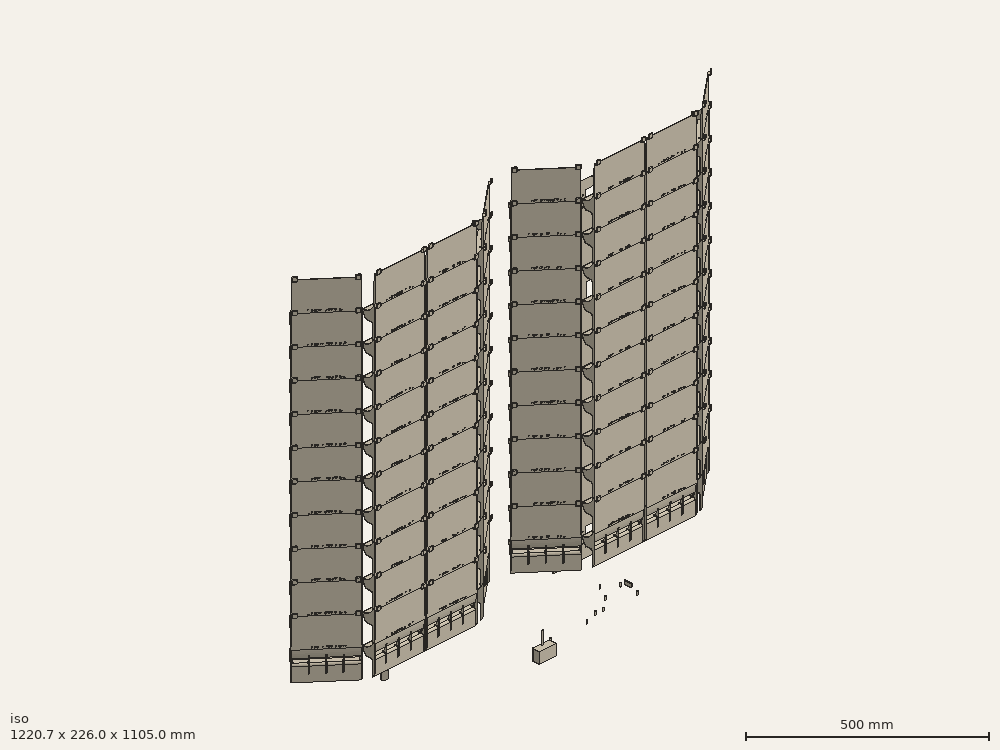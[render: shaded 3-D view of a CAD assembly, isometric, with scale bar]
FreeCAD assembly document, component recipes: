
FREECAD ASSEMBLY — COMPONENT RECIPES ("composit_stand11")

This assembly document has 29 components, labeled P0..P28 below (a component is one placed body or linked part). 28 of them carry a construction recipe — the FreeCAD feature program that regenerates the part from scratch, quoted from this document or its linked companion documents; the rest are supplied as boundary geometry only. No exploded tour is included for this assembly.
NOTE — this tour is split across 2 documents so each fits a 32k-token context. This is document 1: the component sections continue in the remaining 1 document, each repeating the header above.
COMPONENT P0 — recipe-attached ("dropper_fix_composit", modeled in this document).
Construction recipe (the document's own serialized feature program — sketch geometry with constraints, then the solid features built on it; lengths are millimeters unless a unit is written):

FEATURE [PartDesign::SubShapeBinder] Binder003
  BindCopyOnChange = 0
  BindMode = 0
  ClaimChildren = true
  Context = -> Body002 [Binder003.]
  Fuse = false
  MakeFace = true
  OffsetFill = false
  OffsetIntersection = false
  OffsetJoinType = 0
  OffsetOpenResult = false
  PartialLoad = false
  Relative = true
  Support = -> [Connect001]
  _Version = 2
FEATURE [PartDesign::FeaturePython] BaseBend001  # WARN: FeaturePython — macro-defined, semantics opaque (R4)
  BendSide = 0
  BendSketch = -> Binder003
  MidPlane = false
  Reverse = false
  Suppressed = false
  length = 100
  radius = 0.1
  thickness = 0.3
FEATURE [PartDesign::FeaturePython] Extend001  # WARN: FeaturePython — macro-defined, semantics opaque (R4)
  BaseFeature = -> BaseBend001
  Offset = 0.02
  Refine = true
  Suppressed = false
  UseSubtraction = false
  baseObject = -> BaseBend001 [Face1]
  gap1 = 0
  gap2 = 0
  length = 0
FEATURE [PartDesign::FeaturePython] Bend001  # WARN: FeaturePython — macro-defined, semantics opaque (R4)
  AutoMiter = true
  BaseFeature = -> Extend001
  BendType = 1
  LengthList = [15]
  LengthSpec = 0
  ReliefFactor = 0.7
  Suppressed = false
  UseReliefFactor = false
  angle = 90
  baseObject = -> Extend001 [Edge6,Edge8,Edge9,Edge11]
  bendAList = [90]
  extend1 = 0
  extend2 = 0
  gap1 = 0
  gap2 = 0
  invert = true
  kfactor = 0.5
  length = 15
  maxExtendDist = 5
  minGap = 0.2
  minReliefGap = 1
  miterangle1 = 0
  miterangle2 = 0
  offset = 0
  radius = 0.1
  reliefType = 0
  reliefd = 1
  reliefw = 0.8
  sketchflip = false
  sketchinvert = false
  unfold = false
  expr: radius = BaseBend.radius
FEATURE [Sketcher::SketchObject] Sketch031
  AttachmentSupport = -> [XY_Plane003]
  ExternalGeometry = -> [Binder003]
  FullyConstrained = true
  MapMode = 5
  sketch-geometry (13):
    g0: LineSegment StartX=172.194 StartY=8.2 StartZ=0 EndX=172.194 EndY=11.2 EndZ=0
    g1: LineSegment StartX=172.194 StartY=11.2 StartZ=0 EndX=174.122 EndY=8.90187 EndZ=0
    g2: LineSegment StartX=172.194 StartY=8.2 StartZ=0 EndX=173.286 EndY=8.2 EndZ=0
    g3: LineSegment StartX=173.286 StartY=8.2 StartZ=0 EndX=174.122 EndY=8.90187 EndZ=0
    g4: LineSegment StartX=309.163 StartY=122.737 StartZ=0 EndX=309.163 EndY=147 EndZ=0
    g5: LineSegment StartX=309.163 StartY=122.214 StartZ=0 EndX=312.42 EndY=124.947 EndZ=0
    g6: LineSegment StartX=309.163 StartY=122.214 StartZ=0 EndX=308.906 EndY=122.521 EndZ=0
    g7: LineSegment StartX=308.906 StartY=122.521 StartZ=0 EndX=309.163 EndY=122.737 EndZ=0
    g8: LineSegment StartX=312.163 StartY=150 StartZ=0 EndX=312.163 EndY=125.254 EndZ=0
    g9: LineSegment StartX=312.163 StartY=125.254 StartZ=0 EndX=312.42 EndY=124.947 EndZ=0
    g10: LineSegment StartX=309.163 StartY=147 StartZ=0 EndX=311.763 EndY=147 EndZ=0
    g11: LineSegment StartX=311.763 StartY=147 StartZ=0 EndX=311.763 EndY=150 EndZ=0
    g12: LineSegment StartX=311.763 StartY=150 StartZ=0 EndX=312.163 EndY=150 EndZ=0
  constraints (38):
    c: PointOnObject(g0,g-3)
    c: Coincident(g0,g1)
    c: PointOnObject(g1,g-4)
    c: Perpendicular(g-3,g0)
    c: Perpendicular(g-4,g1)
    c: Equal(g1,g0)
    c: DistanceY(g0,g0) = 3
    c: Coincident(g0,g2)
    c: Coincident(g2,g-4)
    c: Coincident(g2,g3)
    c: Coincident(g3,g1)
    c: Vertical(g4)
    c: Coincident(g4,g10)
    c: Coincident(g12,g8)
    c: PointOnObject(g5,g-4)
    c: Vertical(g4,g5)
    c: Coincident(g5,g6)
    c: Coincident(g6,g7)
    c: Distance(g6) = 0.4
    c: Perpendicular(g5,g6)
    c: Perpendicular(g7,g6)
    c: DistanceX(g10,g12) = 3
    c: Coincident(g5,g9)
    c: Coincident(g7,g4)
    c: Coincident(g8,g9)
    c: Vertical(g8)
    c: Perpendicular(g5,g9)
    c: PointOnObject(g-5,g5)
    c: Distance(g9) = 0.4
    c: Coincident(g10,g11)
    c: Horizontal(g10)
    c: Coincident(g11,g12)
    c: Horizontal(g12)
    c: Coincident(g8,g-5)
    c: Vertical(g11)
    c: DistanceY(g11,g11) = 3
    c: DistanceX(g12,g12) = 0.4
    c: Distance(g8,g4) = 3
FEATURE [PartDesign::Pocket] Pocket003
  BaseFeature = -> Bend001
  Direction = (0,0,-1)
  Length = 5
  Length2 = 5
  Midplane = true
  Profile = -> Sketch031
  ReferenceAxis = -> Sketch031 [N_Axis]
  Suppressed = false
  Type = 1
FEATURE [PartDesign::Mirrored] Mirrored
  BaseFeature = -> Pocket003
  MirrorPlane = -> Sketch031 [V_Axis]
  Originals = -> [Pocket003]
  Suppressed = false
FEATURE [PartDesign::CoordinateSystem] Local_CS008
  AttacherType = Attacher::AttachEngine3D
  AttachmentOffset = pos=(0,20,0) rot=(0,0,1;0rad)
  AttachmentSupport = -> [XY_Plane003]
  MapMode = 5
  Placement = pos=(0,20,0) rot=(0,0,1;0rad)
  expr: .AttachmentOffset.Base.y = <<base_Sketch>>.Constraints.offset
FEATURE [PartDesign::CoordinateSystem] Local_CS013  label="dropper_fix_PP_placement"
  AttacherType = Attacher::AttachEngine3D
  AttachmentOffset = pos=(0,0,3) rot=(0,0,1;0rad)
  AttachmentSupport = -> [XY_Plane003]
  MapMode = 5
  Placement = pos=(0,0,3) rot=(0,0,1;0rad)
FEATURE [PartDesign::Boolean] Boolean031
  BaseFeature = -> Mirrored
  Group = -> [Compound039]
  Suppressed = false
  Type = 1
  UsePlacement = true
FEATURE [PartDesign::Boolean] Boolean030
  BaseFeature = -> Boolean031
  Group = -> [Compound038]
  Refine = true
  Suppressed = false
  Type = 0
  UsePlacement = true
FEATURE [PartDesign::Boolean] Boolean002
  BaseFeature = -> Boolean030
  Group = -> [Compound009]
  Suppressed = false
  Type = 1
  UsePlacement = true
FEATURE [PartDesign::Body] Body002  label="dropper_fix_composit"
  Group = -> [Binder003,BaseBend001,Extend001,Sketch031,Bend001,Pocket003,Mirrored,Boolean031,Boolean030,Boolean002,Local_CS008,Local_CS013]
  Origin = -> Origin003
  Tip = -> Boolean002
COMPONENT P1 — recipe-attached ("sink", modeled in this document).
Construction recipe (the document's own serialized feature program — sketch geometry with constraints, then the solid features built on it; lengths are millimeters unless a unit is written):

FEATURE [PartDesign::SubShapeBinder] Binder001
  BindCopyOnChange = 0
  BindMode = 0
  ClaimChildren = true
  Context = -> Body003 [Binder001.]
  Fuse = false
  MakeFace = true
  OffsetFill = false
  OffsetIntersection = false
  OffsetJoinType = 0
  OffsetOpenResult = false
  PartialLoad = false
  Relative = false
  Support = -> [Sketch]
  _Version = 2
FEATURE [PartDesign::CoordinateSystem] Local_CS
  AttacherType = Attacher::AttachEngine3D
  AttachmentOffset = pos=(0,0,0) rot=(0,1,0;1.5708rad)
  MapMode = 7
  Placement = pos=(164.635,-1.4e-14,0) rot=(0.889126,0.323616,0.323616;1.68804rad)
FEATURE [Sketcher::SketchObject] Sketch005  label="sink_side_line"
  ExternalGeometry = -> [Binder001]
  FullyConstrained = true
  MapMode = 5
  Placement = pos=(164.635,-2.8e-14,0) rot=(0.889126,0.323616,0.323616;1.68804rad)
  sketch-geometry (1):
    g0: LineSegment StartX=-2.84e-14 StartY=0 StartZ=0 EndX=202.244 EndY=20 EndZ=0
  constraints (4):
    c: Coincident(g0,g-3)
    c: Vertical(g0,g-3)
    c: DistanceY(g0) = 20  'height'
    c: Angle(g0) = 0.0985699  'angle'
FEATURE [Sketcher::SketchObject] Sketch006  label="sink_front_bend_sketch"
  ExternalGeometry = -> [Sketch005]
  FullyConstrained = true
  MapMode = 5
  Placement = pos=(0,0,0) rot=(0.57735,0.57735,0.57735;2.0944rad)
  sketch-geometry (3):
    g0: LineSegment StartX=0 StartY=2.91403 StartZ=0 EndX=-1.83e-14 EndY=0 EndZ=0
    g1: LineSegment StartX=-1.83e-14 StartY=0 StartZ=0 EndX=2.88014 EndY=0.443099 EndZ=0
    g2: ArcOfCircle CenterX=2.5 CenterY=2.91403 CenterZ=0 NormalX=0 NormalY=0 NormalZ=1 AngleXU=0 Radius=2.5 StartAngle=3.14159 EndAngle=4.86504
  constraints (8):
    c: PointOnObject(g0,g-2)
    c: Coincident(g0,g-3)
    c: Coincident(g0,g1)
    c: PointOnObject(g1,g-3)
    c: Tangent(g2,g1) = -1.5708
    c: Tangent(g2,g0) = -1.5708
    c: Radius(g2) = 2.5
    c: Angle(g1) = 0.152649  'angle'
FEATURE [Sketcher::SketchObject] Sketch007
  ExternalGeometry = -> [Binder001]
  FullyConstrained = true
  MapMode = 7
  Placement = pos=(164.635,-8.5e-14,-4e-15) rot=(0.846388,-0.394677,-0.357572;1.83324rad)
  sketch-geometry (3):
    g0: ArcOfCircle CenterX=-2.5 CenterY=2.81034 CenterZ=0 NormalX=0 NormalY=0 NormalZ=1 AngleXU=0 Radius=2.5 StartAngle=4.59564 EndAngle=6.28319
    g1: LineSegment StartX=-2.79121 StartY=0.327355 StartZ=0 EndX=0 EndY=0 EndZ=0
    g2: LineSegment StartX=0 StartY=0 StartZ=0 EndX=0 EndY=2.81034 EndZ=0
  constraints (7):
    c: PointOnObject(g0,g-2)
    c: Coincident(g1,g-1)
    c: Coincident(g2,g1)
    c: Tangent(g2,g0) = -1.5708
    c: Tangent(g1,g0) = -1.5708
    c: PointOnObject(g0,g-3)
    c: Radius(g0) = 2.5
FEATURE [PartDesign::CoordinateSystem] Local_CS001
  AttacherType = Attacher::AttachEngine3D
  AttachmentOffset = pos=(0,0,0) rot=(1,0,0;0.152649rad)
  MapMode = 5
  Placement = pos=(0,0,0) rot=(1,0,0;0.152649rad)
  expr: .AttachmentOffset.Rotation.Angle = <<sink_front_bend_sketch>>.Constraints.angle
FEATURE [Sketcher::SketchObject] Sketch008  label="sink_plane_sketch"
  ExternalGeometry = -> [Sketch006,Sketch005,Sketch007]
  FullyConstrained = true
  MapMode = 5
  Placement = pos=(0,0,0) rot=(1,0,0;0.152649rad)
  sketch-geometry (4):
    g0: LineSegment StartX=-163.725 StartY=2.91403 StartZ=0 EndX=163.725 EndY=2.91403 EndZ=0
    g1: LineSegment StartX=163.725 StartY=2.91403 StartZ=0 EndX=317.576 EndY=133.529 EndZ=0
    g2: LineSegment StartX=317.576 StartY=133.529 StartZ=0 EndX=-317.576 EndY=133.529 EndZ=0
    g3: LineSegment StartX=-317.576 StartY=133.529 StartZ=0 EndX=-163.725 EndY=2.91403 EndZ=0
  constraints (14):
    c: Coincident(g0,g1)
    c: Coincident(g1,g2)
    c: Coincident(g2,g3)
    c: Coincident(g3,g0)
    c: Symmetric(g0,g0,g-2)
    c: Symmetric(g2,g1,g-2)
    c: Parallel(g1,g-4)
    c: PointOnObject(g-5,g1)
    c: PointOnObject(g-3,g0)
    c: Distance(g1) = 201.818  'rigth_side'
    c: Distance(g0) = 327.45  'front'
    c: Distance(g2) = 635.153  'end'
    c: Distance(g3) = 201.818  'left_side'
    c: DistanceY(g-4,g1) = 2
FEATURE [Sketcher::SketchObject] Sketch009
  ExternalGeometry = -> [Sketch006]
  FullyConstrained = true
  MapMode = 2
  Placement = pos=(0,0,0) rot=(0.57735,0.57735,0.57735;2.0944rad)
  sketch-geometry (4):
    g0: ArcOfCircle CenterX=2.5 CenterY=2.91403 CenterZ=0 NormalX=0 NormalY=0 NormalZ=1 AngleXU=0 Radius=2.5 StartAngle=3.14159 EndAngle=4.86504
    g1: LineSegment StartX=2.88014 StartY=0.443099 StartZ=0 EndX=2.80411 EndY=0.937285 EndZ=0
    g2: LineSegment StartX=1.1302e-12 StartY=2.91403 StartZ=0 EndX=0.5 EndY=2.91403 EndZ=0
    g3: ArcOfCircle CenterX=2.5 CenterY=2.91403 CenterZ=0 NormalX=0 NormalY=0 NormalZ=1 AngleXU=0 Radius=2 StartAngle=3.14159 EndAngle=4.86504
  constraints (10):
    c: Coincident(g0,g-3)
    c: Tangent(g0,g-3) = -1.5708
    c: Coincident(g0,g1)
    c: Coincident(g0,g2)
    c: Coincident(g3,g0)
    c: Coincident(g3,g2)
    c: Coincident(g3,g1)
    c: Perpendicular(g3,g1)
    c: Perpendicular(g3,g2)
    c: Distance(g1) = 0.5
FEATURE [Sketcher::SketchObject] Sketch010
  ExternalGeometry = -> [Sketch007]
  FullyConstrained = true
  MapMode = 7
  Placement = pos=(163.725,2.88014,0.443099) rot=(0.846388,-0.394677,-0.357572;1.83324rad)
  sketch-geometry (4):
    g0: ArcOfCircle CenterX=0.291206 CenterY=2.48298 CenterZ=0 NormalX=0 NormalY=0 NormalZ=1 AngleXU=0 Radius=2.5 StartAngle=4.59564 EndAngle=6.28319
    g1: LineSegment StartX=-2.56e-14 StartY=2.7e-15 StartZ=0 EndX=0.0582413 EndY=0.496596 EndZ=0
    g2: LineSegment StartX=2.79121 StartY=2.48298 StartZ=0 EndX=2.29121 EndY=2.48298 EndZ=0
    g3: ArcOfCircle CenterX=0.291206 CenterY=2.48298 CenterZ=0 NormalX=0 NormalY=0 NormalZ=1 AngleXU=0 Radius=2 StartAngle=4.59564 EndAngle=6.28319
  constraints (10):
    c: Coincident(g0,g-3)
    c: Tangent(g0,g-3) = -1.5708
    c: Coincident(g1,g0)
    c: Coincident(g2,g0)
    c: Coincident(g3,g0)
    c: Coincident(g3,g1)
    c: Coincident(g3,g2)
    c: Perpendicular(g0,g1)
    c: Perpendicular(g0,g2)
    c: Distance(g1) = 0.5
FEATURE [Sketcher::SketchObject] Sketch011
  ExternalGeometry = -> [Sketch008]
  FullyConstrained = true
  MapMode = 7
  Placement = pos=(-163.725,2.88014,0.443099) rot=(-0.298783,0.640743,0.707232;3.7787rad)
  sketch-geometry (4):
    g0: ArcOfCircle CenterX=0.291206 CenterY=2.48298 CenterZ=0 NormalX=0 NormalY=0 NormalZ=1 AngleXU=0 Radius=2 StartAngle=4.59564 EndAngle=6.28319
    g1: ArcOfCircle CenterX=0.291206 CenterY=2.48298 CenterZ=0 NormalX=0 NormalY=0 NormalZ=1 AngleXU=0 Radius=2.5 StartAngle=4.59564 EndAngle=6.28319
    g2: LineSegment StartX=-4e-16 StartY=0 StartZ=0 EndX=0.0582413 EndY=0.496596 EndZ=0
    g3: LineSegment StartX=2.29121 StartY=2.48298 StartZ=0 EndX=2.79121 EndY=2.48298 EndZ=0
  constraints (12):
    c: Coincident(g1,g0)
    c: Coincident(g1,g-1)
    c: Coincident(g2,g1)
    c: Coincident(g2,g0)
    c: Coincident(g3,g0)
    c: Coincident(g3,g1)
    c: Perpendicular(g0,g3)
    c: Perpendicular(g0,g2)
    c: Perpendicular(g2,g-3)
    c: Horizontal(g3)
    c: Radius(g0) = 2
    c: Distance(g2) = 0.5
FEATURE [PartDesign::Pad] Pad
  Direction = (0,-0.152057,0.988372)
  Length = 0.5
  Length2 = 10
  Placement = pos=(0,0,0) rot=(1,0,0;0.152649rad)
  Profile = -> Sketch008
  ReferenceAxis = -> Sketch008 [N_Axis]
  Suppressed = false
  Type = 0
FEATURE [PartDesign::Pad] Pad001
  BaseFeature = -> Pad
  Direction = (-0.762326,-0.639667,-0.0984104)
  Length = 201.818
  Length2 = 10
  Placement = pos=(0,0,0) rot=(1,0,0;0.152649rad)
  Profile = -> Sketch010
  ReferenceAxis = -> Sketch010 [N_Axis]
  Reversed = true
  Suppressed = false
  Type = 0
  expr: Length = <<sink_plane_sketch>>.Constraints.rigth_side
FEATURE [PartDesign::Pad] Pad002
  BaseFeature = -> Pad001
  Direction = (-0.762326,0.639667,0.0984104)
  Length = 201.818
  Length2 = 10
  Placement = pos=(0,0,0) rot=(1,0,0;0.152649rad)
  Profile = -> Sketch011
  ReferenceAxis = -> Sketch011 [N_Axis]
  Suppressed = false
  Type = 0
  expr: Length = <<sink_plane_sketch>>.Constraints.left_side
FEATURE [PartDesign::Pad] Pad003
  BaseFeature = -> Pad002
  Direction = (1,0,0)
  Length = 327.45
  Length2 = 10
  Midplane = true
  Placement = pos=(0,0,0) rot=(1,0,0;0.152649rad)
  Profile = -> Sketch009
  ReferenceAxis = -> Sketch009 [N_Axis]
  Suppressed = false
  Type = 0
  expr: Length = <<sink_plane_sketch>>.Constraints.front
FEATURE [Sketcher::SketchObject] Sketch013
  ExternalGeometry = -> [Sketch008,Sketch009]
  FullyConstrained = true
  MapMode = 5
  Placement = pos=(0,0,0) rot=(1,0,0;1.5708rad)
  sketch-geometry (6):
    g0: LineSegment StartX=-163.725 StartY=2.91403 StartZ=0 EndX=-163.725 EndY=80 EndZ=0
    g1: LineSegment StartX=-163.725 StartY=80 StartZ=0 EndX=163.725 EndY=80 EndZ=0
    g2: LineSegment StartX=163.725 StartY=80 StartZ=0 EndX=163.725 EndY=2.91403 EndZ=0
    g3: LineSegment StartX=163.725 StartY=2.91403 StartZ=0 EndX=-163.725 EndY=2.91403 EndZ=0
    g4: LineSegment StartX=-163.725 StartY=0.443099 StartZ=0 EndX=-163.725 EndY=2.91403 EndZ=0
    g5: LineSegment StartX=163.725 StartY=0.443099 StartZ=0 EndX=163.725 EndY=2.91403 EndZ=0
  constraints (16):
    c: Vertical(g0)
    c: Coincident(g0,g1)
    c: Horizontal(g1)
    c: Coincident(g1,g2)
    c: Vertical(g2)
    c: Coincident(g2,g3)
    c: Coincident(g3,g0)
    c: Horizontal(g3)
    c: PointOnObject(g-4,g3)
    c: Coincident(g4,g-3)
    c: Coincident(g4,g0)
    c: Perpendicular(g3,g4)
    c: Coincident(g5,g-3)
    c: Coincident(g5,g2)
    c: Perpendicular(g3,g5)
    c: DistanceY(g1) = 80
FEATURE [Sketcher::SketchObject] Sketch012
  ExternalGeometry = -> [Sketch008,Sketch010,Sketch013]
  FullyConstrained = true
  MapMode = 5
  Placement = pos=(164.635,-2.8e-14,0) rot=(0.889126,0.323616,0.323616;1.68804rad)
  sketch-geometry (4):
    g0: LineSegment StartX=0.909926 StartY=2.91403 StartZ=0 EndX=201.749 EndY=22.775 EndZ=0
    g1: LineSegment StartX=0.909926 StartY=2.91403 StartZ=0 EndX=0.909926 EndY=80 EndZ=0
    g2: LineSegment StartX=0.909926 StartY=80 StartZ=0 EndX=201.749 EndY=80 EndZ=0
    g3: LineSegment StartX=201.749 StartY=80 StartZ=0 EndX=201.749 EndY=22.775 EndZ=0
  constraints (11):
    c: Coincident(g0,g-4)
    c: Parallel(g-3,g0)
    c: Equal(g0,g-3)
    c: Coincident(g0,g1)
    c: Vertical(g1)
    c: Coincident(g1,g2)
    c: Horizontal(g2)
    c: Coincident(g2,g3)
    c: Coincident(g3,g0)
    c: Vertical(g3)
    c: Horizontal(g-5,g1)
FEATURE [PartDesign::Pad] Pad004
  BaseFeature = -> Pad003
  Direction = (0,-1,2e-16)
  Length = 0.5
  Length2 = 10
  Placement = pos=(0,0,0) rot=(1,0,0;0.152649rad)
  Profile = -> Sketch013
  ReferenceAxis = -> Sketch013 [N_Axis]
  Reversed = true
  Suppressed = false
  Type = 0
FEATURE [PartDesign::Pad] Pad005
  BaseFeature = -> Pad004
  Direction = (0.642788,-0.766044,0)
  Length = 0.5
  Length2 = 10
  Placement = pos=(0,0,0) rot=(1,0,0;0.152649rad)
  Profile = -> Sketch012
  ReferenceAxis = -> Sketch012 [N_Axis]
  Reversed = true
  Suppressed = false
  Type = 0
FEATURE [Sketcher::SketchObject] Sketch014
  ExternalGeometry = -> [Binder001]
  FullyConstrained = true
  MapMode = 5
  sketch-geometry (1):
    g0: LineSegment StartX=-319.563 StartY=130 StartZ=0 EndX=-164.635 EndY=0 EndZ=0
  constraints (2):
    c: Symmetric(g0,g-3,g-2)
    c: Symmetric(g0,g-3,g-2)
FEATURE [PartDesign::CoordinateSystem] Local_CS003
  AttacherType = Attacher::AttachEngine3D
  AttachmentOffset = pos=(0,0,0) rot=(0,1,0;1.5708rad)
  MapMode = 7
  Placement = pos=(-164.635,-1.4e-14,0) rot=(0.889126,-0.323616,-0.323616;1.68804rad)
FEATURE [Sketcher::SketchObject] Sketch015
  ExternalGeometry = -> [Sketch008,Sketch011,Sketch013]
  FullyConstrained = true
  MapMode = 5
  Placement = pos=(-164.635,-2.8e-14,0) rot=(0.889126,-0.323616,-0.323616;1.68804rad)
  sketch-geometry (5):
    g0: LineSegment StartX=-201.749 StartY=22.775 StartZ=0 EndX=-0.909926 EndY=2.91403 EndZ=0
    g1: LineSegment StartX=-0.909926 StartY=2.91403 StartZ=0 EndX=-0.909926 EndY=80 EndZ=0
    g2: LineSegment StartX=-0.909926 StartY=80 StartZ=0 EndX=-201.749 EndY=80 EndZ=0
    g3: LineSegment StartX=-201.749 StartY=80 StartZ=0 EndX=-201.749 EndY=22.775 EndZ=0
    g4: LineSegment StartX=-201.993 StartY=20.3041 StartZ=0 EndX=-201.749 EndY=22.775 EndZ=0
  constraints (13):
    c: Coincident(g0,g-4)
    c: Coincident(g1,g0)
    c: Vertical(g1)
    c: Coincident(g1,g2)
    c: Horizontal(g2)
    c: Coincident(g2,g3)
    c: Coincident(g3,g0)
    c: Vertical(g3)
    c: Coincident(g4,g-3)
    c: Coincident(g4,g0)
    c: Perpendicular(g-3,g4)
    c: Parallel(g-3,g0)
    c: Horizontal(g1,g-5)
FEATURE [PartDesign::Pad] Pad006
  BaseFeature = -> Pad005
  Direction = (-0.642788,-0.766044,0)
  Length = 0.5
  Length2 = 10
  Placement = pos=(0,0,0) rot=(1,0,0;0.152649rad)
  Profile = -> Sketch015
  ReferenceAxis = -> Sketch015 [N_Axis]
  Reversed = true
  Suppressed = false
  Type = 0
FEATURE [Sketcher::SketchObject] Sketch016
  ExternalGeometry = -> [Pad006]
  FullyConstrained = true
  MapMode = 5
  Placement = pos=(0,0,0) rot=(1,0,0;0.152649rad)
  sketch-geometry (28):
    g0: LineSegment StartX=0 StartY=2 StartZ=0 EndX=40.9313 EndY=2 EndZ=0
    g1: LineSegment StartX=40.9313 StartY=2 StartZ=0 EndX=81.8625 EndY=2 EndZ=0
    g2: LineSegment StartX=81.8625 StartY=2 StartZ=0 EndX=122.794 EndY=2 EndZ=0
    g3: LineSegment StartX=122.794 StartY=2 StartZ=0 EndX=163.725 EndY=2 EndZ=0
    g4: ArcOfCircle CenterX=-17 CenterY=2 CenterZ=0 NormalX=0 NormalY=0 NormalZ=1 AngleXU=0 Radius=3 StartAngle=1.5708 EndAngle=4.71239
    g5: ArcOfCircle CenterX=17 CenterY=2 CenterZ=0 NormalX=0 NormalY=0 NormalZ=1 AngleXU=0 Radius=3 StartAngle=4.71239 EndAngle=7.85398
    g6: LineSegment StartX=-17 StartY=5 StartZ=0 EndX=17 EndY=5 EndZ=0
    g7: LineSegment StartX=-17 StartY=-1 StartZ=0 EndX=17 EndY=-1 EndZ=0
    g8: GeomPoint X=-20 Y=2 Z=0
    g9: GeomPoint X=20 Y=2 Z=0
    g10: ArcOfCircle CenterX=106 CenterY=2 CenterZ=0 NormalX=0 NormalY=0 NormalZ=1 AngleXU=0 Radius=3 StartAngle=1.5708 EndAngle=4.71239
    g11: ArcOfCircle CenterX=140 CenterY=2 CenterZ=0 NormalX=0 NormalY=0 NormalZ=1 AngleXU=0 Radius=3 StartAngle=4.71239 EndAngle=7.85398
    g12: LineSegment StartX=106 StartY=5 StartZ=0 EndX=140 EndY=5 EndZ=0
    g13: LineSegment StartX=106 StartY=-1 StartZ=0 EndX=140 EndY=-1 EndZ=0
    g14: ArcOfCircle CenterX=-140 CenterY=2 CenterZ=0 NormalX=0 NormalY=0 NormalZ=1 AngleXU=0 Radius=3 StartAngle=1.5708 EndAngle=4.71239
    g15: ArcOfCircle CenterX=-106 CenterY=2 CenterZ=0 NormalX=0 NormalY=0 NormalZ=1 AngleXU=0 Radius=3 StartAngle=4.71239 EndAngle=7.85398
    g16: LineSegment StartX=-140 StartY=5 StartZ=0 EndX=-106 EndY=5 EndZ=0
    g17: LineSegment StartX=-140 StartY=-1 StartZ=0 EndX=-106 EndY=-1 EndZ=0
    g18: ArcOfCircle CenterX=-78.5 CenterY=2 CenterZ=0 NormalX=0 NormalY=0 NormalZ=1 AngleXU=0 Radius=3 StartAngle=1.5708 EndAngle=4.71239
    g19: ArcOfCircle CenterX=-44.5 CenterY=2 CenterZ=0 NormalX=0 NormalY=0 NormalZ=1 AngleXU=0 Radius=3 StartAngle=4.71239 EndAngle=7.85398
    g20: LineSegment StartX=-78.5 StartY=5 StartZ=0 EndX=-44.5 EndY=5 EndZ=0
    g21: LineSegment StartX=-78.5 StartY=-1 StartZ=0 EndX=-44.5 EndY=-1 EndZ=0
    g22: ArcOfCircle CenterX=44.5 CenterY=2 CenterZ=0 NormalX=0 NormalY=0 NormalZ=1 AngleXU=0 Radius=3 StartAngle=1.5708 EndAngle=4.71239
    g23: ArcOfCircle CenterX=78.5 CenterY=2 CenterZ=0 NormalX=0 NormalY=0 NormalZ=1 AngleXU=0 Radius=3 StartAngle=4.71239 EndAngle=7.85398
    g24: LineSegment StartX=44.5 StartY=5 StartZ=0 EndX=78.5 EndY=5 EndZ=0
    g25: LineSegment StartX=44.5 StartY=-1 StartZ=0 EndX=78.5 EndY=-1 EndZ=0
    g26: LineSegment StartX=17 StartY=-1 StartZ=0 EndX=44.5 EndY=-1 EndZ=0
    g27: LineSegment StartX=78.5 StartY=-1 StartZ=0 EndX=106 EndY=-1 EndZ=0
  constraints (67):
    c: PointOnObject(g0,g-2)
    c: Coincident(g0,g1)
    c: Horizontal(g1)
    c: Coincident(g1,g2)
    c: Coincident(g2,g3)
    c: Horizontal(g3)
    c: Vertical(g-3,g3)
    c: Horizontal(g0)
    c: Equal(g0,g1)
    c: Equal(g1,g2)
    c: Equal(g2,g3)
    c: DistanceY(g0) = 2
    c: Horizontal(g2)
    c: Tangent(g4,g6) = 1.5708
    c: Tangent(g4,g7) = -1.5708
    c: Tangent(g5,g6) = 1.5708
    c: Tangent(g5,g7) = -1.5708
    c: Equal(g4,g5)
    c: PointOnObject(g5,g0)
    c: Symmetric(g4,g5,g-2)
    c: Radius(g5) = 3
    c: PointOnObject(g8,g4)
    c: PointOnObject(g9,g5)
    c: Horizontal(g9,g8)
    c: Horizontal(g8,g0)
    c: DistanceX(g8,g9) = 40
    c: Tangent(g10,g12) = 1.5708
    c: Tangent(g10,g13) = -1.5708
    c: Tangent(g11,g12) = 1.5708
    c: Tangent(g11,g13) = -1.5708
    c: Equal(g10,g11)
    c: Tangent(g14,g16) = 1.5708
    c: Tangent(g14,g17) = -1.5708
    c: Tangent(g15,g16) = 1.5708
    c: Tangent(g15,g17) = -1.5708
    c: Equal(g14,g15)
    c: Tangent(g18,g20) = 1.5708
    c: Tangent(g18,g21) = -1.5708
    c: Tangent(g19,g20) = 1.5708
    c: Tangent(g19,g21) = -1.5708
    c: Equal(g18,g19)
    c: Tangent(g22,g24) = 1.5708
    c: Tangent(g22,g25) = -1.5708
    c: Tangent(g23,g24) = 1.5708
    c: Tangent(g23,g25) = -1.5708
    c: Equal(g22,g23)
    c: Horizontal(g14,g15)
    c: Horizontal(g18,g19)
    c: Horizontal(g22,g23)
    c: Horizontal(g10,g11)
    c: Equal(g11,g23)
    c: Equal(g23,g5)
    c: Equal(g5,g19)
    c: Equal(g19,g15)
    c: Equal(g16,g20)
    c: Equal(g20,g6)
    c: Equal(g6,g24)
    c: Equal(g12,g24)
    c: Horizontal(g10,g22)
    c: Symmetric(g19,g22,g-2)
    c: Symmetric(g10,g15,g-2)
    c: Tangent(g26,g5) = -1.5708
    c: Coincident(g26,g22)
    c: Coincident(g27,g23)
    c: Coincident(g27,g10)
    c: Equal(g26,g27)
    c: DistanceX(g11) = 140
FEATURE [PartDesign::FeaturePython] SketchOnSheet  # WARN: FeaturePython — macro-defined, semantics opaque (R4)
  BaseFeature = -> Pad006
  Sketch = -> Sketch016
  Suppressed = false
  baseObject = -> Pad006 [Face14]
  kfactor = 0.5
FEATURE [PartDesign::FeaturePython] CornerRelief  # WARN: FeaturePython — macro-defined, semantics opaque (R4)
  BaseFeature = -> SketchOnSheet
  ReliefSketch = 0
  Size = 5
  SizeRatio = 1
  Suppressed = false
  XOffset = 0
  YOffset = 0
  baseObject = -> SketchOnSheet [Edge56,Edge57]
  kfactor = 0.5
FEATURE [PartDesign::FeaturePython] CornerRelief001  # WARN: FeaturePython — macro-defined, semantics opaque (R4)
  BaseFeature = -> CornerRelief
  ReliefSketch = 0
  Size = 5
  SizeRatio = 1
  Suppressed = false
  XOffset = 0
  YOffset = 0
  baseObject = -> CornerRelief [Edge17,Edge14]
  kfactor = 0.5
  expr: Size = <<CornerRelief>>.Size
FEATURE [Sketcher::SketchObject] Sketch017
  ExternalGeometry = -> [Sketch012]
  FullyConstrained = true
  MapMode = 5
  Placement = pos=(164.635,-2.8e-14,0) rot=(0.889126,0.323616,0.323616;1.68804rad)
  sketch-geometry (6):
    g0: LineSegment StartX=0.909926 StartY=78 StartZ=0 EndX=0.909926 EndY=80 EndZ=0
    g1: LineSegment StartX=0.909926 StartY=80 StartZ=0 EndX=2.90993 EndY=80 EndZ=0
    g2: LineSegment StartX=199.749 StartY=80 StartZ=0 EndX=201.749 EndY=80 EndZ=0
    g3: LineSegment StartX=201.749 StartY=80 StartZ=0 EndX=201.749 EndY=78 EndZ=0
    g4: ArcOfCircle CenterX=2.90993 CenterY=78 CenterZ=0 NormalX=0 NormalY=0 NormalZ=1 AngleXU=0 Radius=2 StartAngle=1.5708 EndAngle=3.14159
    g5: ArcOfCircle CenterX=199.749 CenterY=78 CenterZ=0 NormalX=0 NormalY=0 NormalZ=1 AngleXU=0 Radius=2 StartAngle=5.856e-13 EndAngle=1.5708
  constraints (14):
    c: Coincident(g0,g-3)
    c: Vertical(g0)
    c: Coincident(g0,g1)
    c: PointOnObject(g1,g-3)
    c: Coincident(g2,g-3)
    c: Coincident(g2,g3)
    c: Tangent(g5,g3) = 1.5708
    c: Tangent(g5,g2) = 1.5708
    c: Tangent(g4,g1) = 1.5708
    c: Tangent(g4,g0) = 1.5708
    c: Equal(g4,g5)
    c: Radius(g5) = 2
    c: Vertical(g3)
    c: PointOnObject(g2,g-3)
FEATURE [Sketcher::SketchObject] Sketch018
  ExternalGeometry = -> [Sketch015]
  FullyConstrained = true
  MapMode = 2
  Placement = pos=(-164.635,-2.8e-14,0) rot=(0.889126,-0.323616,-0.323616;1.68804rad)
  sketch-geometry (6):
    g0: ArcOfCircle CenterX=-2.90993 CenterY=78 CenterZ=0 NormalX=0 NormalY=0 NormalZ=1 AngleXU=0 Radius=2 StartAngle=6.28318 EndAngle=7.85398
    g1: ArcOfCircle CenterX=-199.749 CenterY=78 CenterZ=0 NormalX=0 NormalY=0 NormalZ=1 AngleXU=0 Radius=2 StartAngle=1.5708 EndAngle=3.14159
    g2: LineSegment StartX=-201.749 StartY=78 StartZ=0 EndX=-201.749 EndY=80 EndZ=0
    g3: LineSegment StartX=-201.749 StartY=80 StartZ=0 EndX=-199.749 EndY=80 EndZ=0
    g4: LineSegment StartX=-2.90993 StartY=80 StartZ=0 EndX=-0.909926 EndY=80 EndZ=0
    g5: LineSegment StartX=-0.909926 StartY=80 StartZ=0 EndX=-0.909926 EndY=78 EndZ=0
  constraints (15):
    c: PointOnObject(g1,g-3)
    c: Coincident(g2,g3)
    c: Vertical(g2)
    c: Tangent(g1,g2) = 1.5708
    c: Tangent(g3,g1) = 1.5708
    c: Coincident(g4,g5)
    c: Coincident(g5,g0)
    c: Tangent(g5,g0)
    c: Tangent(g0,g4) = 1.5708
    c: Coincident(g4,g-3)
    c: Equal(g0,g1)
    c: Radius(g0) = 2
    c: Coincident(g2,g-3)
    c: PointOnObject(g0,g-3)
    c: Vertical(g5)
FEATURE [Sketcher::SketchObject] Sketch019
  ExternalGeometry = -> [Sketch013]
  FullyConstrained = true
  MapMode = 5
  Placement = pos=(0,0,0) rot=(1,0,0;1.5708rad)
  sketch-geometry (6):
    g0: LineSegment StartX=161.725 StartY=80 StartZ=0 EndX=163.725 EndY=80 EndZ=0
    g1: LineSegment StartX=163.725 StartY=80 StartZ=0 EndX=163.725 EndY=78 EndZ=0
    g2: LineSegment StartX=-163.725 StartY=78 StartZ=0 EndX=-163.725 EndY=80 EndZ=0
    g3: LineSegment StartX=-163.725 StartY=80 StartZ=0 EndX=-161.725 EndY=80 EndZ=0
    g4: ArcOfCircle CenterX=-161.725 CenterY=78 CenterZ=0 NormalX=0 NormalY=0 NormalZ=1 AngleXU=0 Radius=2 StartAngle=1.5708 EndAngle=3.14159
    g5: ArcOfCircle CenterX=161.725 CenterY=78 CenterZ=0 NormalX=0 NormalY=0 NormalZ=1 AngleXU=0 Radius=2 StartAngle=5.87e-13 EndAngle=1.5708
  constraints (14):
    c: Coincident(g0,g-3)
    c: Coincident(g0,g1)
    c: Coincident(g2,g-3)
    c: Coincident(g2,g3)
    c: Tangent(g5,g1) = 1.5708
    c: Tangent(g5,g0) = 1.5708
    c: Tangent(g4,g2) = 1.5708
    c: Tangent(g4,g3) = 1.5708
    c: Equal(g5,g4)
    c: Radius(g5) = 2
    c: PointOnObject(g3,g-3)
    c: Vertical(g2)
    c: PointOnObject(g0,g-3)
    c: Vertical(g1)
FEATURE [PartDesign::Pocket] Pocket
  BaseFeature = -> CornerRelief001
  Direction = (-0.642788,0.766044,0)
  Length = 5
  Length2 = 5
  Midplane = true
  Profile = -> Sketch017
  ReferenceAxis = -> Sketch017 [N_Axis]
  Suppressed = false
  Type = 1
FEATURE [PartDesign::Pocket] Pocket001
  BaseFeature = -> Pocket
  Direction = (0.642788,0.766044,-3e-16)
  Length = 5
  Length2 = 5
  Midplane = true
  Profile = -> Sketch018
  ReferenceAxis = -> Sketch018 [N_Axis]
  Suppressed = false
  Type = 0
FEATURE [PartDesign::Pocket] Pocket002
  BaseFeature = -> Pocket001
  Direction = (0,1,-2e-16)
  Length = 5
  Length2 = 5
  Midplane = true
  Profile = -> Sketch019
  ReferenceAxis = -> Sketch019 [N_Axis]
  Suppressed = false
  Type = 1
FEATURE [PartDesign::CoordinateSystem] Local_CS004  label="sink_place"
  AttacherType = Attacher::AttachEngine3D
  MapMode = 5
FEATURE [Sketcher::SketchObject] Sketch054
  ExternalGeometry = -> [Sketch008]
  FullyConstrained = true
  MapMode = 5
  Placement = pos=(0,0,0) rot=(0.57735,0.57735,0.57735;2.0944rad)
  sketch-geometry (7):
    g0: ArcOfCircle CenterX=132.281 CenterY=18.3274 CenterZ=0 NormalX=0 NormalY=0 NormalZ=1 AngleXU=0 Radius=2 StartAngle=0 EndAngle=1.72345
    g1: ArcOfCircle CenterX=132.281 CenterY=18.3274 CenterZ=0 NormalX=0 NormalY=0 NormalZ=1 AngleXU=0 Radius=2.5 StartAngle=1.4e-15 EndAngle=1.72345
    g2: LineSegment StartX=131.977 StartY=20.3041 StartZ=0 EndX=131.901 EndY=20.7983 EndZ=0
    g3: LineSegment StartX=134.281 StartY=18.3274 StartZ=0 EndX=134.281 EndY=10.8274 EndZ=0
    g4: LineSegment StartX=134.281 StartY=10.8274 StartZ=0 EndX=134.781 EndY=10.8274 EndZ=0
    g5: LineSegment StartX=134.781 StartY=10.8274 StartZ=0 EndX=134.781 EndY=18.3274 EndZ=0
    g6: LineSegment StartX=134.781 StartY=20.8274 StartZ=0 EndX=0 EndY=20.8274 EndZ=0
  constraints (19):
    c: Coincident(g1,g0)
    c: Coincident(g2,g1)
    c: Vertical(g3)
    c: Coincident(g4,g3)
    c: Horizontal(g4)
    c: Coincident(g5,g4)
    c: Vertical(g5)
    c: Tangent(g0,g-3) = 1.5708
    c: Perpendicular(g2,g-3)
    c: Distance(g2) = 0.5
    c: Coincident(g2,g0)
    c: Radius(g0) = 2
    c: Horizontal(g6)
    c: Tangent(g6,g1)
    c: PointOnObject(g6,g-2)
    c: PointOnObject(g6,g5)
    c: Tangent(g3,g0) = 1.5708
    c: DistanceY(g4,g6) = 10
    c: Tangent(g5,g1) = -1.5708
FEATURE [PartDesign::Pad] Pad017
  BaseFeature = -> Pocket002
  Direction = (1,0,0)
  Length = 635.153
  Length2 = 10
  Midplane = true
  Profile = -> Sketch054
  ReferenceAxis = -> Sketch054 [N_Axis]
  Suppressed = false
  Type = 0
  expr: Length = <<sink_plane_sketch>>.Constraints.end
FEATURE [Sketcher::SketchObject] Sketch055
  ExternalGeometry = -> [Sketch054]
  FullyConstrained = true
  MapMode = 5
  Placement = pos=(0,0,0) rot=(1,0,0;1.5708rad)
  expr: Constraints[5] = <<sink_plane_sketch>>.Constraints.end / 2
  sketch-geometry (3):
    g0: ArcOfCircle CenterX=315.576 CenterY=12.8274 CenterZ=0 NormalX=0 NormalY=0 NormalZ=1 AngleXU=0 Radius=2 StartAngle=4.71239 EndAngle=6.28319
    g1: LineSegment StartX=315.576 StartY=10.8274 StartZ=0 EndX=317.576 EndY=10.8274 EndZ=0
    g2: LineSegment StartX=317.576 StartY=10.8274 StartZ=0 EndX=317.576 EndY=12.8274 EndZ=0
  constraints (9):
    c: Coincident(g1,g2)
    c: Coincident(g2,g0)
    c: Tangent(g2,g0)
    c: Vertical(g2)
    c: Horizontal(g1)
    c: DistanceX(g1) = 317.576
    c: Radius(g0) = 2
    c: Tangent(g0,g1) = -1.5708
    c: Horizontal(g-3,g1)
FEATURE [PartDesign::Pocket] Pocket006
  BaseFeature = -> Pad017
  Direction = (0,1,-2e-16)
  Length = 5
  Length2 = 5
  Midplane = true
  Profile = -> Sketch055
  ReferenceAxis = -> Sketch055 [N_Axis]
  Suppressed = false
  Type = 1
FEATURE [PartDesign::Mirrored] Mirrored002
  BaseFeature = -> Pocket006
  MirrorPlane = -> Sketch055 [V_Axis]
  Originals = -> [Pocket006]
  Suppressed = false
FEATURE [PartDesign::Boolean] Boolean006
  BaseFeature = -> Mirrored002
  Group = -> [Compound014]
  Suppressed = false
  Type = 1
  UsePlacement = true
FEATURE [PartDesign::Body] Body003  label="sink"
  Group = -> [Binder001,Local_CS,Sketch005,Sketch006,Sketch007,Local_CS001,Sketch008,Sketch009,Sketch010,Sketch011,Pad,Pad001,Pad002,Pad003,Sketch012,Sketch013,Pad004,Pad005,Sketch014,Local_CS003,Sketch015,Pad006,Sketch016,SketchOnSheet,CornerRelief,CornerRelief001,Sketch017,Sketch018,Sketch019,Pocket,Pocket001,Pocket002,Local_CS004,Sketch054,Pad017,Sketch055,Pocket006,Mirrored002,Boolean006]
  Origin = -> Origin004
  Tip = -> Mirrored002
COMPONENT P2 — recipe-attached ("dropper_fix_PP", modeled in this document).
Construction recipe (the document's own serialized feature program — sketch geometry with constraints, then the solid features built on it; lengths are millimeters unless a unit is written):

FEATURE [PartDesign::SubShapeBinder] Binder007
  BindCopyOnChange = 0
  BindMode = 0
  ClaimChildren = true
  Context = -> Body004 [Binder007.]
  Fuse = false
  MakeFace = true
  OffsetFill = false
  OffsetIntersection = false
  OffsetJoinType = 0
  OffsetOpenResult = false
  PartialLoad = false
  Relative = true
  Support = -> [Connect004]
  _Version = 2
FEATURE [PartDesign::Pad] Pad007
  Direction = (0,0,1)
  Length = 5
  Length2 = 10
  Profile = -> Binder007
  Suppressed = false
  Type = 0
FEATURE [PartDesign::CoordinateSystem] Local_CS012
  AttacherType = Attacher::AttachEngine3D
  AttachmentSupport = -> [XY_Plane005]
  MapMode = 5
FEATURE [PartDesign::Boolean] Boolean003
  BaseFeature = -> Pad007
  Group = -> [Fusion]
  Suppressed = false
  Type = 1
  UsePlacement = true
FEATURE [PartDesign::Body] Body004  label="dropper_fix_PP"
  Group = -> [Binder007,Pad007,Boolean003,Local_CS012]
  Origin = -> Origin005
  Tip = -> Boolean003
COMPONENT P3 — recipe-attached ("bar", modeled in this document).
Construction recipe (the document's own serialized feature program — sketch geometry with constraints, then the solid features built on it; lengths are millimeters unless a unit is written):

FEATURE [PartDesign::SubShapeBinder] Binder008
  BindCopyOnChange = 0
  BindMode = 0
  ClaimChildren = true
  Context = -> Body005 [Binder008.]
  Fuse = false
  MakeFace = true
  OffsetFill = false
  OffsetIntersection = false
  OffsetJoinType = 0
  OffsetOpenResult = false
  PartialLoad = false
  Relative = false
  Support = -> [Connect005]
  _Version = 2
FEATURE [PartDesign::Pad] Pad008  label="bar_pad"
  Direction = (0,0,1)
  Length = 1272.25
  Length2 = 10
  Profile = -> Binder008
  Refine = true
  Suppressed = false
  Type = 0
  expr: Length = <<Dimensions>>.Constraints.width - 3 mm * 2
FEATURE [PartDesign::CoordinateSystem] Local_CS016  label="bar_orig"
  AttacherType = Attacher::AttachEngine3D
  MapMode = 5
FEATURE [PartDesign::CoordinateSystem] Local_CS018  label="bar_top"
  AttacherType = Attacher::AttachEngine3D
  AttachmentOffset = pos=(0,0,1272.25) rot=(0,-1,0;3.14159rad)
  MapMode = 5
  Placement = pos=(0,0,1272.25) rot=(0,1,0;3.14159rad)
  expr: .AttachmentOffset.Base.z = <<bar_pad>>.Length
FEATURE [Sketcher::SketchObject] Sketch057
  FullyConstrained = true
  MapMode = 5
  Placement = pos=(0,0,0) rot=(1,0,0;1.5708rad)
  expr: Constraints[6] = <<bar_base_sketch>>.Constraints.total_width / 2
  sketch-geometry (3):
    g0: ArcOfCircle CenterX=25 CenterY=5 CenterZ=0 NormalX=0 NormalY=0 NormalZ=1 AngleXU=0 Radius=5 StartAngle=4.71239 EndAngle=6.28319
    g1: LineSegment StartX=25 StartY=3.304e-13 StartZ=0 EndX=30 EndY=0 EndZ=0
    g2: LineSegment StartX=30 StartY=0 StartZ=0 EndX=30 EndY=5 EndZ=0
  constraints (8):
    c: PointOnObject(g0,g-1)
    c: PointOnObject(g1,g-1)
    c: Coincident(g2,g1)
    c: Tangent(g2,g0) = -1.5708
    c: Vertical(g2)
    c: Tangent(g1,g0) = -1.5708
    c: DistanceX(g1) = 30
    c: Radius(g0) = 5
FEATURE [PartDesign::Plane] DatumPlane001
  AttachmentOffset = pos=(0,0,636.126) rot=(0,0,1;0rad)
  Length = 70.9545
  MapMode = 5
  Placement = pos=(0,0,636.126) rot=(0,0,1;0rad)
  ResizeMode = 0
  Width = 60.9545
  expr: .AttachmentOffset.Base.z = <<bar_pad>>.Length / 2
FEATURE [PartDesign::Mirrored] Mirrored003
  MirrorPlane = -> YZ_Plane006
  Suppressed = false
FEATURE [PartDesign::Mirrored] Mirrored004
  MirrorPlane = -> DatumPlane001
  Suppressed = false
FEATURE [Sketcher::SketchObject] Sketch058
  AttachmentOffset = pos=(0,240.563,0) rot=(0,0,1;0rad)
  FullyConstrained = true
  MapMode = 5
  Placement = pos=(0,5.3e-14,240.563) rot=(1,0,0;1.5708rad)
  expr: .AttachmentOffset.Base.y = <<Dimensions>>.Constraints.module_middle_side - 3 mm - <<Dimensions>>.Constraints.module_center_offset
  expr: Constraints[44] = -<<bar_base_sketch>>.Constraints.total_width / 2
  sketch-geometry (22):
    g0: LineSegment StartX=-21 StartY=61.5 StartZ=0 EndX=-21 EndY=70.5 EndZ=0
    g1: LineSegment StartX=-30 StartY=76.5 StartZ=0 EndX=-30 EndY=55.5 EndZ=0
    g2: LineSegment StartX=-21 StartY=-70.5 StartZ=0 EndX=-21 EndY=-61.5 EndZ=0
    g3: LineSegment StartX=-30 StartY=-55.5 StartZ=0 EndX=-30 EndY=-76.5 EndZ=0
    g4: LineSegment StartX=-24 StartY=-58.5 StartZ=0 EndX=-27 EndY=-58.5 EndZ=0
    g5: LineSegment StartX=-27 StartY=58.5 StartZ=0 EndX=-24 EndY=58.5 EndZ=0
    g6: LineSegment StartX=-24 StartY=73.5 StartZ=0 EndX=-27 EndY=73.5 EndZ=0
    g7: LineSegment StartX=-27 StartY=-73.5 StartZ=0 EndX=-24 EndY=-73.5 EndZ=0
    g8: ArcOfCircle CenterX=-27 CenterY=76.5 CenterZ=0 NormalX=0 NormalY=0 NormalZ=1 AngleXU=0 Radius=3 StartAngle=3.14159 EndAngle=4.71239
    g9: ArcOfCircle CenterX=-27 CenterY=55.5 CenterZ=0 NormalX=0 NormalY=0 NormalZ=1 AngleXU=0 Radius=3 StartAngle=1.5708 EndAngle=3.14159
    g10: ArcOfCircle CenterX=-27 CenterY=-55.5 CenterZ=0 NormalX=0 NormalY=0 NormalZ=1 AngleXU=0 Radius=3 StartAngle=3.14159 EndAngle=4.71239
    g11: ArcOfCircle CenterX=-27 CenterY=-76.5 CenterZ=0 NormalX=0 NormalY=0 NormalZ=1 AngleXU=0 Radius=3 StartAngle=1.5708 EndAngle=3.14159
    g12: ArcOfCircle CenterX=-24 CenterY=61.5 CenterZ=0 NormalX=0 NormalY=0 NormalZ=1 AngleXU=0 Radius=3 StartAngle=4.71239 EndAngle=6.28319
    g13: GeomPoint X=-21 Y=58.5 Z=0
    g14: ArcOfCircle CenterX=-24 CenterY=70.5 CenterZ=0 NormalX=0 NormalY=0 NormalZ=1 AngleXU=0 Radius=3 StartAngle=1.6e-15 EndAngle=1.5708
    g15: GeomPoint X=-21 Y=73.5 Z=0
    g16: ArcOfCircle CenterX=-24 CenterY=-61.5 CenterZ=0 NormalX=0 NormalY=0 NormalZ=1 AngleXU=0 Radius=3 StartAngle=9e-16 EndAngle=1.5708
    g17: GeomPoint X=-21 Y=-58.5 Z=0
    g18: ArcOfCircle CenterX=-24 CenterY=-70.5 CenterZ=0 NormalX=0 NormalY=0 NormalZ=1 AngleXU=0 Radius=3 StartAngle=4.71239 EndAngle=6.28319
    g19: GeomPoint X=-21 Y=-73.5 Z=0
    g20: GeomPoint X=-30 Y=66 Z=0
    g21: GeomPoint X=-30 Y=-66 Z=0
  constraints (49):
    c: Vertical(g0)
    c: Vertical(g1)
    c: Vertical(g2)
    c: Vertical(g3)
    c: Equal(g3,g1)
    c: Symmetric(g3,g1,g-1)
    c: Horizontal(g4)
    c: Horizontal(g5)
    c: Horizontal(g6)
    c: Horizontal(g7)
    c: Tangent(g11,g7) = 1.5708
    c: Tangent(g11,g3) = -1.5708
    c: Tangent(g10,g4) = 1.5708
    c: Tangent(g10,g3) = -1.5708
    c: Tangent(g9,g5) = 1.5708
    c: Tangent(g9,g1) = -1.5708
    c: Tangent(g8,g6) = 1.5708
    c: Tangent(g8,g1) = -1.5708
    c: PointOnObject(g13,g0)
    c: PointOnObject(g13,g5)
    c: Tangent(g0,g12) = -1.5708
    c: Tangent(g5,g12) = -1.5708
    c: PointOnObject(g15,g0)
    c: PointOnObject(g15,g6)
    c: Tangent(g0,g14) = -1.5708
    c: Tangent(g6,g14) = -1.5708
    c: PointOnObject(g17,g2)
    c: PointOnObject(g17,g4)
    c: Tangent(g2,g16) = -1.5708
    c: Tangent(g4,g16) = -1.5708
    c: PointOnObject(g19,g2)
    c: PointOnObject(g19,g7)
    c: Tangent(g2,g18) = -1.5708
    c: Tangent(g7,g18) = -1.5708
    c: Equal(g18,g11)
    c: Equal(g11,g16)
    c: Equal(g16,g10)
    c: Equal(g10,g9)
    c: Equal(g9,g12)
    c: Equal(g12,g14)
    c: Equal(g14,g8)
    c: Radius(g14) = 3
    c: Symmetric(g3,g3,g21)
    c: Symmetric(g1,g1,g20)
    c: DistanceX(g20) = -30
    c: Vertical(g17,g13)
    c: DistanceY(g19,g17) = 15
    c: DistanceY(g21,g20) = 132
    c: Distance(g15,g1) = 9
FEATURE [PartDesign::Boolean] Boolean004
  BaseFeature = -> Pad008
  Group = -> [Compound012]
  Refine = true
  Suppressed = false
  Type = 1
  UsePlacement = true
FEATURE [PartDesign::Pocket] Pocket007
  BaseFeature = -> Boolean004
  Direction = (0,1,-2e-16)
  Length = 5
  Length2 = 5
  Profile = -> Sketch057
  ReferenceAxis = -> Sketch057 [N_Axis]
  Suppressed = false
  Type = 1
FEATURE [PartDesign::MultiTransform] MultiTransform
  BaseFeature = -> Pocket007
  Originals = -> [Pocket007]
  Suppressed = false
  Transformations = -> [Mirrored003,Mirrored004]
FEATURE [Sketcher::SketchObject] Sketch113
  AttachmentOffset = pos=(0,97,0) rot=(0,0,1;0rad)
  FullyConstrained = true
  MapMode = 5
  Placement = pos=(0,2.2e-14,97) rot=(1,0,0;1.5708rad)
  sketch-geometry (10):
    g0: LineSegment StartX=-18.1 StartY=-50 StartZ=0 EndX=-13 EndY=-50 EndZ=0
    g1: LineSegment StartX=-11 StartY=-48 StartZ=0 EndX=-11 EndY=48 EndZ=0
    g2: LineSegment StartX=-13 StartY=50 StartZ=0 EndX=-18.1 EndY=50 EndZ=0
    g3: LineSegment StartX=-20.1 StartY=48 StartZ=0 EndX=-20.1 EndY=-48 EndZ=0
    g4: ArcOfCircle CenterX=-18.1 CenterY=-48 CenterZ=0 NormalX=0 NormalY=0 NormalZ=1 AngleXU=0 Radius=2 StartAngle=3.14159 EndAngle=4.71239
    g5: ArcOfCircle CenterX=-13 CenterY=-48 CenterZ=0 NormalX=0 NormalY=0 NormalZ=1 AngleXU=0 Radius=2 StartAngle=4.71239 EndAngle=6.28319
    g6: ArcOfCircle CenterX=-13 CenterY=48 CenterZ=0 NormalX=0 NormalY=0 NormalZ=1 AngleXU=0 Radius=2 StartAngle=7e-16 EndAngle=1.5708
    g7: ArcOfCircle CenterX=-18.1 CenterY=48 CenterZ=0 NormalX=0 NormalY=0 NormalZ=1 AngleXU=0 Radius=2 StartAngle=1.5708 EndAngle=3.14159
    g8: GeomPoint X=-20.1 Y=-50 Z=0
    g9: GeomPoint X=-11 Y=50 Z=0
  constraints (23):
    c: Tangent(g0,g4) = -1.5708
    c: Tangent(g0,g5) = -1.5708
    c: Tangent(g1,g5) = -1.5708
    c: Tangent(g1,g6) = -1.5708
    c: Tangent(g2,g6) = -1.5708
    c: Tangent(g2,g7) = -1.5708
    c: Tangent(g3,g7) = -1.5708
    c: Tangent(g3,g4) = -1.5708
    c: Horizontal(g0)
    c: Horizontal(g2)
    c: Vertical(g1)
    c: Vertical(g3)
    c: Equal(g4,g5)
    c: Equal(g6,g7)
    c: PointOnObject(g8,g0)
    c: PointOnObject(g8,g3)
    c: PointOnObject(g9,g1)
    c: PointOnObject(g9,g2)
    c: DistanceX(g2) = -13
    c: DistanceX(g2) = -18.1
    c: Radius(g6) = 2
    c: Symmetric(g5,g6,g-1)
    c: DistanceY(g8,g9) = 100
FEATURE [PartDesign::Pocket] Pocket032
  BaseFeature = -> MultiTransform
  Direction = (0,1,-2e-16)
  Length = 5
  Length2 = 5
  Profile = -> Sketch113
  ReferenceAxis = -> Sketch113 [N_Axis]
  Suppressed = false
  Type = 1
FEATURE [PartDesign::LinearPattern] LinearPattern
  BaseFeature = -> Pocket032
  Direction = -> Sketch113 [V_Axis]
  Length = 1078.25
  Mode = 0
  Occurrences = 2
  Offset = 1078.25
  Originals = -> [Pocket032]
  Suppressed = false
  expr: Length = <<bar_pad>>.Length - <<Sketch113>>.AttachmentOffset.Base.y * 2
FEATURE [PartDesign::Body] Body005  label="bar"
  Group = -> [Binder008,Pad008,Boolean004,Local_CS016,Local_CS018,Sketch057,Pocket007,DatumPlane001,MultiTransform,Mirrored003,Mirrored004,Sketch058,Sketch113,Pocket032,LinearPattern]
  Origin = -> Origin006
  Tip = -> LinearPattern
COMPONENT P4 — recipe-attached ("bar_fix", modeled in this document).
Construction recipe (the document's own serialized feature program — sketch geometry with constraints, then the solid features built on it; lengths are millimeters unless a unit is written):

FEATURE [PartDesign::SubShapeBinder] Binder009
  BindCopyOnChange = 0
  BindMode = 0
  ClaimChildren = true
  Context = -> Body006 [Binder009.]
  Fuse = false
  MakeFace = true
  OffsetFill = false
  OffsetIntersection = false
  OffsetJoinType = 0
  OffsetOpenResult = false
  PartialLoad = false
  Placement = pos=(0,0,0) rot=(0.57735,0.57735,0.57735;2.0944rad)
  Relative = false
  Support = -> [Sketch035]
  _Version = 2
FEATURE [PartDesign::FeaturePython] BaseBend002  label="bar_fix_BaseBend"  # WARN: FeaturePython — macro-defined, semantics opaque (R4)
  BendSide = 1
  BendSketch = -> Binder009
  MidPlane = true
  Reverse = false
  Suppressed = false
  length = 26
  radius = 2
  thickness = 0.7
  expr: length = <<bar_base_sketch>>.Constraints.inner_plane_width
FEATURE [PartDesign::CoordinateSystem] Local_CS017  label="bar_fix_orig"
  AttacherType = Attacher::AttachEngine3D
  AttachmentOffset = pos=(0,0,0) rot=(0,0,1;3.14159rad)
  MapMode = 5
  Placement = pos=(0,0,0) rot=(0,0,1;3.14159rad)
FEATURE [Sketcher::SketchObject] Sketch059
  AttachmentOffset = pos=(13,40,0) rot=(0,0,1;0rad)
  FullyConstrained = true
  MapMode = 5
  Placement = pos=(13,8.9e-15,40) rot=(1,0,0;1.5708rad)
  expr: .AttachmentOffset.Base.x = <<bar_fix_BaseBend>>.length / 2
  expr: .AttachmentOffset.Base.y = <<bar_fix_base_sketch>>.Constraints.bar_side
  sketch-geometry (3):
    g0: ArcOfCircle CenterX=-5 CenterY=-5 CenterZ=0 NormalX=0 NormalY=0 NormalZ=1 AngleXU=0 Radius=5 StartAngle=-2.7e-15 EndAngle=1.5708
    g1: LineSegment StartX=-5 StartY=0 StartZ=0 EndX=0 EndY=0 EndZ=0
    g2: LineSegment StartX=0 StartY=0 StartZ=0 EndX=0 EndY=-5 EndZ=0
  constraints (7):
    c: PointOnObject(g0,g-1)
    c: PointOnObject(g0,g-2)
    c: Coincident(g1,g-1)
    c: Coincident(g2,g1)
    c: Tangent(g2,g0) = 1.5708
    c: Tangent(g1,g0) = 1.5708
    c: Radius(g0) = 5
FEATURE [PartDesign::Pocket] Pocket009
  BaseFeature = -> BaseBend002
  Direction = (0,1,-2e-16)
  Length = 5
  Length2 = 5
  Midplane = true
  Profile = -> Sketch059
  ReferenceAxis = -> Sketch059 [N_Axis]
  Suppressed = false
  Type = 1
FEATURE [Sketcher::SketchObject] Sketch060
  AttachmentOffset = pos=(13,50,0) rot=(0,0,1;0rad)
  FullyConstrained = true
  MapMode = 5
  Placement = pos=(13,50,0) rot=(0,0,1;0rad)
  expr: .AttachmentOffset.Base.x = <<bar_fix_BaseBend>>.length / 2
  expr: .AttachmentOffset.Base.y = <<bar_fix_base_sketch>>.Constraints.comp_side
  sketch-geometry (3):
    g0: LineSegment StartX=-5 StartY=0 StartZ=0 EndX=0 EndY=0 EndZ=0
    g1: LineSegment StartX=0 StartY=0 StartZ=0 EndX=0 EndY=-5 EndZ=0
    g2: ArcOfCircle CenterX=-5 CenterY=-5 CenterZ=0 NormalX=0 NormalY=0 NormalZ=1 AngleXU=0 Radius=5 StartAngle=0 EndAngle=1.5708
  constraints (7):
    c: PointOnObject(g0,g-1)
    c: Coincident(g0,g-1)
    c: Coincident(g0,g1)
    c: PointOnObject(g1,g-2)
    c: Tangent(g2,g0) = 1.5708
    c: Tangent(g2,g1) = 1.5708
    c: Radius(g2) = 5
FEATURE [PartDesign::Pocket] Pocket010
  BaseFeature = -> Pocket009
  Direction = (0,0,-1)
  Length = 5
  Length2 = 5
  Midplane = true
  Profile = -> Sketch060
  ReferenceAxis = -> Sketch060 [N_Axis]
  Suppressed = false
  Type = 1
FEATURE [PartDesign::Mirrored] Mirrored005
  BaseFeature = -> Pocket010
  MirrorPlane = -> YZ_Plane007
  Originals = -> [Pocket009,Pocket010]
  Suppressed = false
FEATURE [PartDesign::Boolean] Boolean005
  BaseFeature = -> Mirrored005
  Group = -> [Compound013]
  Suppressed = false
  Type = 1
  UsePlacement = true
FEATURE [PartDesign::Body] Body006  label="bar_fix"
  Group = -> [Binder009,BaseBend002,Sketch059,Pocket009,Sketch060,Pocket010,Mirrored005,Boolean005,Local_CS017]
  Origin = -> Origin007
  Tip = -> Boolean005
COMPONENT P5 — recipe-attached ("sink_back", modeled in this document).
Construction recipe (the document's own serialized feature program — sketch geometry with constraints, then the solid features built on it; lengths are millimeters unless a unit is written):

FEATURE [PartDesign::CoordinateSystem] Local_CS020
  AttacherType = Attacher::AttachEngine3D
  AttachmentOffset = pos=(0,3,0) rot=(0,0,1;0rad)
  AttachmentSupport = -> [XY_Plane008]
  MapMode = 5
  Placement = pos=(0,3,0) rot=(0,0,1;0rad)
FEATURE [PartDesign::SubShapeBinder] Binder010
  BindCopyOnChange = 0
  BindMode = 0
  ClaimChildren = true
  Context = -> Body007 [Binder010.]
  Fuse = false
  MakeFace = true
  OffsetFill = false
  OffsetIntersection = false
  OffsetJoinType = 0
  OffsetOpenResult = false
  PartialLoad = false
  Placement = pos=(0,0,0) rot=(1,0,0;1.5708rad)
  Relative = false
  Support = -> [Sketch040]
  _Version = 2
FEATURE [Sketcher::SketchObject] Sketch042  label="sink_back_base_Sketch"
  ExternalGeometry = -> [Binder010]
  FullyConstrained = false
  MapMode = 5
  Placement = pos=(0,0,0) rot=(0.57735,0.57735,0.57735;2.0944rad)
  sketch-geometry (11):
    g0: LineSegment StartX=0 StartY=-33.9589 StartZ=0 EndX=7.8e-15 EndY=35 EndZ=0
    g1: LineSegment StartX=7.8e-15 StartY=35 StartZ=0 EndX=-0.5 EndY=35 EndZ=0
    g2: LineSegment StartX=-0.5 StartY=35 StartZ=0 EndX=-0.5 EndY=-33.9589 EndZ=0
    g3: LineSegment StartX=0.566059 StartY=-36.0067 StartZ=0 EndX=3.27471 EndY=-37.9034 EndZ=0
    g4: LineSegment StartX=3.27471 StartY=-37.9034 StartZ=0 EndX=3.5615 EndY=-37.4938 EndZ=0
    g5: LineSegment StartX=3.5615 StartY=-37.4938 StartZ=0 EndX=0.852847 EndY=-35.5972 EndZ=0
    g6: ArcOfCircle CenterX=2 CenterY=-33.9589 CenterZ=0 NormalX=0 NormalY=0 NormalZ=1 AngleXU=0 Radius=2 StartAngle=3.14159 EndAngle=4.10152
    g7: GeomPoint X=0 Y=-35 Z=0
    g8: ArcOfCircle CenterX=2 CenterY=-33.9589 CenterZ=0 NormalX=0 NormalY=0 NormalZ=1 AngleXU=0 Radius=2.5 StartAngle=3.14159 EndAngle=4.10152
    g9: GeomPoint X=-0.5 Y=-35.2603 Z=0
    g10: LineSegment StartX=0.566059 StartY=-36.0067 StartZ=0 EndX=0.852847 EndY=-35.5972 EndZ=0
  constraints (26):
    c: PointOnObject(g7,g-2)
    c: Coincident(g0,g1)
    c: Horizontal(g1)
    c: Coincident(g1,g2)
    c: Vertical(g2)
    c: Coincident(g3,g4)
    c: Coincident(g4,g5)
    c: PointOnObject(g7,g0)
    c: PointOnObject(g7,g5)
    c: Tangent(g0,g6) = 1.5708
    c: Tangent(g5,g6) = 1.5708
    c: PointOnObject(g9,g2)
    c: PointOnObject(g9,g3)
    c: Tangent(g2,g8) = -1.5708
    c: Tangent(g3,g8) = -1.5708
    c: Coincident(g8,g6)
    c: DistanceX(g1,g1) = 0.5
    c: Perpendicular(g5,g4)
    c: Perpendicular(g3,g4)
    c: Radius(g6) = 2
    c: Angle(g5) = 2.53073
    c: Coincident(g10,g8)
    c: Angle(g5,g-1) = 0.610865  'angle'
    c: Coincident(g10,g6)
    c: Coincident(g0,g-4)
    c: PointOnObject(g-3,g5)
FEATURE [Sketcher::SketchObject] Sketch041
  AttachmentOffset = pos=(0,0,-35) rot=(1,0,0;-0.610865rad)
  AttachmentSupport = -> [XY_Plane008]
  ExternalGeometry = -> [Sketch042,Binder010]
  FullyConstrained = true
  MapMode = 5
  Placement = pos=(0,0,-35) rot=(1,0,0;5.67232rad)
  expr: .AttachmentOffset.Rotation.Angle = -<<sink_back_base_Sketch>>.Constraints.angle
  sketch-geometry (4):
    g0: LineSegment StartX=-309.563 StartY=1.04113 StartZ=0 EndX=204.635 EndY=1.04113 EndZ=0
    g1: LineSegment StartX=204.635 StartY=1.04113 StartZ=0 EndX=204.635 EndY=26.0411 EndZ=0
    g2: LineSegment StartX=204.635 StartY=26.0411 StartZ=0 EndX=-309.563 EndY=66.0411 EndZ=0
    g3: LineSegment StartX=-309.563 StartY=66.0411 StartZ=0 EndX=-309.563 EndY=1.04113 EndZ=0
  constraints (13):
    c: Coincident(g0,g1)
    c: Coincident(g1,g2)
    c: Coincident(g2,g3)
    c: Horizontal(g0)
    c: Vertical(g1)
    c: Vertical(g3)
    c: Coincident(g0,g3)
    c: PointOnObject(g-3,g0)
    c: PointOnObject(g-4,g1)
    c: PointOnObject(g-5,g3)
    c: DistanceY(g1,g2) = 40
    c: DistanceY(g1,g1) = 25
    c: Distance(g2) = 515.751  'end'
FEATURE [Sketcher::SketchObject] Sketch043
  AttachmentSupport = -> [Sketch041]
  ExternalGeometry = -> [Sketch041]
  FullyConstrained = true
  MapMode = 7
  Placement = pos=(204.635,21.3316,-49.9366) rot=(0.593097,0.556507,0.581839;2.03146rad)
  sketch-geometry (6):
    g0: LineSegment StartX=2e-16 StartY=-8.9e-15 StartZ=0 EndX=-0.286208 EndY=-0.409982 EndZ=0
    g1: ArcOfCircle CenterX=1.14483 CenterY=1.63993 CenterZ=0 NormalX=0 NormalY=0 NormalZ=1 AngleXU=0 Radius=2 StartAngle=4.10294 EndAngle=5.67374
    g2: ArcOfCircle CenterX=1.14483 CenterY=1.63993 CenterZ=0 NormalX=0 NormalY=0 NormalZ=1 AngleXU=0 Radius=2.5 StartAngle=4.10294 EndAngle=5.67374
    g3: LineSegment StartX=2.78476 StartY=0.495097 StartZ=0 EndX=16.4011 EndY=20 EndZ=0
    g4: LineSegment StartX=16.4011 StartY=20 StartZ=0 EndX=16.8111 EndY=19.7138 EndZ=0
    g5: LineSegment StartX=16.8111 StartY=19.7138 StartZ=0 EndX=3.19474 EndY=0.208889 EndZ=0
  constraints (16):
    c: Coincident(g0,g-3)
    c: Coincident(g1,g0)
    c: Coincident(g2,g1)
    c: Coincident(g2,g0)
    c: Tangent(g1,g3) = -1.5708
    c: Coincident(g3,g4)
    c: Coincident(g4,g5)
    c: Perpendicular(g-3,g0)
    c: Perpendicular(g1,g0)
    c: Tangent(g5,g2) = 1.5708
    c: Distance(g0) = 0.5
    c: Perpendicular(g3,g4)
    c: Perpendicular(g5,g4)
    c: Angle(g3,g-3) = 1.5708
    c: Radius(g1) = 2
    c: DistanceY(g3) = 20
FEATURE [PartDesign::Pad] Pad009  label="sink_back_base_Pad009"
  Direction = (1,0,0)
  Length = 204.635
  Length2 = 309.563
  Placement = pos=(0,0,0) rot=(0.57735,0.57735,0.57735;2.0944rad)
  Profile = -> Sketch042
  ReferenceAxis = -> Sketch042 [N_Axis]
  Suppressed = false
  Type = 4
  expr: Length = <<sink_front_sketch>>.Constraints.right
  expr: Length2 = <<sink_front_sketch>>.Constraints.left
FEATURE [PartDesign::Pad] Pad010
  BaseFeature = -> Pad009
  Direction = (0,0.573576,0.819152)
  Length = 0.5
  Length2 = 10
  Placement = pos=(0,0,0) rot=(0.57735,0.57735,0.57735;2.0944rad)
  Profile = -> Sketch041
  ReferenceAxis = -> Sketch041 [N_Axis]
  Reversed = true
  Suppressed = false
  Type = 0
FEATURE [Sketcher::SketchObject] Sketch061
  AttachmentSupport = -> [XZ_Plane008]
  ExternalGeometry = -> [Sketch042]
  FullyConstrained = true
  MapMode = 5
  Placement = pos=(0,0,0) rot=(1,0,0;1.5708rad)
  expr: Constraints[14] = <<sink_back_base_Pad009>>.Length
  expr: Constraints[15] = -<<sink_back_base_Pad009>>.Length2
  sketch-geometry (6):
    g0: LineSegment StartX=204.635 StartY=30 StartZ=0 EndX=204.635 EndY=35 EndZ=0
    g1: LineSegment StartX=204.635 StartY=35 StartZ=0 EndX=199.635 EndY=35 EndZ=0
    g2: LineSegment StartX=-304.563 StartY=35 StartZ=0 EndX=-309.563 EndY=35 EndZ=0
    g3: LineSegment StartX=-309.563 StartY=35 StartZ=0 EndX=-309.563 EndY=30 EndZ=0
    g4: ArcOfCircle CenterX=199.635 CenterY=30 CenterZ=0 NormalX=0 NormalY=0 NormalZ=1 AngleXU=0 Radius=5 StartAngle=-1.35e-13 EndAngle=1.5708
    g5: ArcOfCircle CenterX=-304.563 CenterY=30 CenterZ=0 NormalX=0 NormalY=0 NormalZ=1 AngleXU=0 Radius=5 StartAngle=1.5708 EndAngle=3.14159
  constraints (16):
    c: Vertical(g0)
    c: Coincident(g0,g1)
    c: Horizontal(g1)
    c: Coincident(g2,g3)
    c: Vertical(g3)
    c: Horizontal(g2)
    c: Horizontal(g2,g0)
    c: Tangent(g5,g2) = -1.5708
    c: Tangent(g5,g3) = -1.5708
    c: Radius(g5) = 5
    c: Tangent(g4,g0) = -1.5708
    c: Tangent(g4,g1) = -1.5708
    c: Equal(g4,g5)
    c: Horizontal(g-3,g0)
    c: DistanceX(g0) = 204.635
    c: DistanceX(g2) = -309.563
FEATURE [Sketcher::SketchObject] Sketch062
  AttachmentSupport = -> [Sketch043]
  FullyConstrained = true
  MapMode = 51
  Placement = pos=(204.79,37.7561,-29.9564) rot=(0.999043,-0.020198,0.0388;4.10074rad)
  expr: Constraints[8] = -<<Pad011>>.Length
  sketch-geometry (6):
    g0: LineSegment StartX=0 StartY=5 StartZ=0 EndX=0 EndY=0 EndZ=0
    g1: LineSegment StartX=0 StartY=0 StartZ=0 EndX=-5 EndY=0 EndZ=0
    g2: LineSegment StartX=-515.751 StartY=5 StartZ=0 EndX=-515.751 EndY=0 EndZ=0
    g3: LineSegment StartX=-515.751 StartY=0 StartZ=0 EndX=-510.751 EndY=0 EndZ=0
    g4: ArcOfCircle CenterX=-5 CenterY=5 CenterZ=0 NormalX=0 NormalY=0 NormalZ=1 AngleXU=0 Radius=5 StartAngle=4.71239 EndAngle=6.28319
    g5: ArcOfCircle CenterX=-510.751 CenterY=5 CenterZ=0 NormalX=0 NormalY=0 NormalZ=1 AngleXU=0 Radius=5 StartAngle=3.14159 EndAngle=4.71239
  constraints (15):
    c: PointOnObject(g0,g-2)
    c: Coincident(g0,g-1)
    c: Coincident(g0,g1)
    c: PointOnObject(g1,g-1)
    c: Vertical(g2)
    c: Coincident(g2,g3)
    c: PointOnObject(g3,g-1)
    c: Horizontal(g3)
    c: DistanceX(g2) = -515.751
    c: Tangent(g4,g0) = 1.5708
    c: Tangent(g4,g1) = 1.5708
    c: Tangent(g5,g3) = -1.5708
    c: Tangent(g5,g2) = -1.5708
    c: Equal(g4,g5)
    c: Radius(g4) = 5
FEATURE [Sketcher::SketchObject] Sketch063
  AttachmentSupport = -> [XZ_Plane008]
  ExternalGeometry = -> [Binder010]
  FullyConstrained = true
  MapMode = 5
  Placement = pos=(0,0,0) rot=(1,0,0;1.5708rad)
  expr: Constraints[1] = -<<Dimensions>>.Constraints.modules_face / 2
  sketch-geometry (10):
    g0: GeomPoint X=-164.635 Y=0 Z=0
    g1: LineSegment StartX=-309.563 StartY=35 StartZ=0 EndX=-309.563 EndY=4.5 EndZ=0
    g2: LineSegment StartX=-307.063 StartY=7 StartZ=0 EndX=-167.135 EndY=7 EndZ=0
    g3: LineSegment StartX=-164.635 StartY=9.5 StartZ=0 EndX=-164.635 EndY=32.5 EndZ=0
    g4: LineSegment StartX=-162.135 StartY=35 StartZ=0 EndX=-309.563 EndY=35 EndZ=0
    g5: ArcOfCircle CenterX=-307.063 CenterY=4.5 CenterZ=0 NormalX=0 NormalY=0 NormalZ=1 AngleXU=0 Radius=2.5 StartAngle=1.5708 EndAngle=3.14159
    g6: ArcOfCircle CenterX=-167.135 CenterY=9.5 CenterZ=0 NormalX=0 NormalY=0 NormalZ=1 AngleXU=0 Radius=2.5 StartAngle=4.71239 EndAngle=6.28319
    g7: ArcOfCircle CenterX=-162.135 CenterY=32.5 CenterZ=0 NormalX=0 NormalY=0 NormalZ=1 AngleXU=0 Radius=2.5 StartAngle=1.5708 EndAngle=3.14159
    g8: GeomPoint X=-309.563 Y=35 Z=0
    g9: GeomPoint X=-164.635 Y=7 Z=0
  constraints (22):
    c: PointOnObject(g0,g-1)
    c: DistanceX(g0) = -164.635
    c: Tangent(g2,g6) = -1.5708
    c: Tangent(g3,g6) = -1.5708
    c: Vertical(g1)
    c: Vertical(g3)
    c: Horizontal(g2)
    c: Horizontal(g4)
    c: Equal(g5,g6)
    c: Equal(g6,g7)
    c: PointOnObject(g9,g2)
    c: PointOnObject(g9,g3)
    c: Diameter(g6) = 5
    c: Vertical(g9,g0)
    c: DistanceY(g0,g9) = 7
    c: Tangent(g7,g3) = 1.5708
    c: Tangent(g4,g7) = -1.5708
    c: Tangent(g5,g2) = 1.5708
    c: Tangent(g5,g1) = -1.5708
    c: Coincident(g8,g-3)
    c: Coincident(g1,g8)
    c: Coincident(g1,g4)
FEATURE [PartDesign::FeaturePython] Bend016  # WARN: FeaturePython — macro-defined, semantics opaque (R4)
  AutoMiter = false
  BaseFeature = -> Pad010
  BendType = 0
  LengthList = [26]
  LengthSpec = 0
  ReliefFactor = 0.7
  Suppressed = false
  UseReliefFactor = false
  angle = 90
  baseObject = -> Pad010 [Edge25]
  bendAList = [90]
  extend1 = 2
  extend2 = 2
  gap1 = 0
  gap2 = 0
  invert = true
  kfactor = 0.5
  length = 26
  maxExtendDist = 5
  minGap = 0.2
  minReliefGap = 1
  miterangle1 = -35
  miterangle2 = 0
  offset = 0
  radius = 1
  reliefType = 0
  reliefd = 1
  reliefw = 0.8
  sketchflip = false
  sketchinvert = false
  unfold = false
  expr: miterangle1 = -<<sink_back_base_Sketch>>.Constraints.angle
FEATURE [Sketcher::SketchObject] Sketch114
  AttachmentOffset = pos=(0,0,205) rot=(0,0,1;0rad)
  AttachmentSupport = -> [YZ_Plane008]
  ExternalGeometry = -> [Sketch043]
  FullyConstrained = true
  MapMode = 5
  Placement = pos=(205,0,0) rot=(0.57735,0.57735,0.57735;2.0944rad)
  expr: Constraints[23] = 90 deg - <<sink_back_base_Sketch>>.Constraints.angle
  sketch-geometry (10):
    g0: LineSegment StartX=-1 StartY=0 StartZ=0 EndX=-1 EndY=-30 EndZ=0
    g1: LineSegment StartX=38.7813 StartY=-30 StartZ=0 EndX=38.7813 EndY=0 EndZ=0
    g2: LineSegment StartX=38.7813 StartY=0 StartZ=0 EndX=-1 EndY=0 EndZ=0
    g3: LineSegment StartX=-1 StartY=-30 StartZ=0 EndX=-0.5 EndY=-30 EndZ=0
    g4: LineSegment StartX=37.7813 StartY=-30 StartZ=0 EndX=38.7813 EndY=-30 EndZ=0
    g5: LineSegment StartX=-0.5 StartY=-30 StartZ=0 EndX=-0.5 EndY=-32 EndZ=0
    g6: LineSegment StartX=1.5 StartY=-30 StartZ=0 EndX=33.9394 EndY=-30 EndZ=0
    g7: LineSegment StartX=35.5777 StartY=-33.1472 StartZ=0 EndX=37.7813 EndY=-30 EndZ=0
    g8: ArcOfCircle CenterX=1.5 CenterY=-32 CenterZ=0 NormalX=0 NormalY=0 NormalZ=1 AngleXU=0 Radius=2 StartAngle=1.5708 EndAngle=3.14159
    g9: ArcOfCircle CenterX=33.9394 CenterY=-32 CenterZ=0 NormalX=0 NormalY=0 NormalZ=1 AngleXU=0 Radius=2 StartAngle=5.67232 EndAngle=7.85398
  constraints (30):
    c: Coincident(g0,g3)
    c: Coincident(g4,g1)
    c: Coincident(g1,g2)
    c: Coincident(g2,g0)
    c: Vertical(g0)
    c: Vertical(g1)
    c: Horizontal(g2)
    c: PointOnObject(g0,g-1)
    c: DistanceX(g0) = -1
    c: DistanceY(g4) = -30
    c: DistanceX(g1) = 38.7813
    c: Coincident(g3,g5)
    c: Horizontal(g3)
    c: Coincident(g7,g4)
    c: Horizontal(g4)
    c: Horizontal(g6)
    c: Horizontal(g0,g6)
    c: Vertical(g5)
    c: Tangent(g8,g5) = -1.5708
    c: Tangent(g8,g6) = 1.5708
    c: DistanceX(g3) = -0.5
    c: Tangent(g9,g6) = 1.5708
    c: Tangent(g9,g7) = -1.5708
    c: Angle(g7) = 0.959931
    c: Equal(g9,g8)
    c: Radius(g9) = 2
    c: Horizontal(g6,g1)
    c: DistanceX(g4) = 37.7813
    c: DistanceX(g4,g4) = 1
    c: DistanceX(g-3,g4) = 0.0252
FEATURE [PartDesign::Pocket] Pocket033
  BaseFeature = -> Bend016
  Direction = (-1,0,0)
  Length = 5
  Length2 = 5
  Profile = -> Sketch114
  ReferenceAxis = -> Sketch114 [N_Axis]
  Reversed = true
  Suppressed = false
  Type = 0
FEATURE [PartDesign::Pad] Pad011
  BaseFeature = -> Pocket033
  Direction = (0.996988,-0.0635308,0.0444847)
  Length = 515.751
  Length2 = 10
  Profile = -> Sketch043
  ReferenceAxis = -> Sketch043 [N_Axis]
  Reversed = true
  Suppressed = false
  Type = 0
  expr: Length = Sketch041.Constraints.end
FEATURE [PartDesign::Pocket] Pocket011
  BaseFeature = -> Pad011
  Direction = (0,1,-2e-16)
  Length = 5
  Length2 = 5
  Midplane = true
  Profile = -> Sketch061
  ReferenceAxis = -> Sketch061 [N_Axis]
  Suppressed = false
  Type = 1
FEATURE [PartDesign::Pocket] Pocket012
  BaseFeature = -> Pocket011
  Direction = (-0.0775567,-0.816685,0.571849)
  Length = 5
  Length2 = 5
  Profile = -> Sketch062
  ReferenceAxis = -> Sketch062 [N_Axis]
  Reversed = true
  Suppressed = false
  Type = 1
FEATURE [PartDesign::Pocket] Pocket013
  BaseFeature = -> Pocket012
  Direction = (0,1,-2e-16)
  Length = 5
  Length2 = 5
  Midplane = true
  Profile = -> Sketch063
  ReferenceAxis = -> Sketch063 [N_Axis]
  Suppressed = false
  Type = 1
FEATURE [PartDesign::Boolean] Boolean007
  BaseFeature = -> Pocket013
  Group = -> [Compound015]
  Suppressed = false
  Type = 1
  UsePlacement = true
FEATURE [PartDesign::Body] Body007  label="sink_back"
  Group = -> [Local_CS020,Binder010,Sketch041,Sketch042,Sketch043,Pad009,Pad010,Bend016,Sketch114,Pocket033,Pad011,Sketch061,Pocket011,Sketch062,Pocket012,Sketch063,Pocket013,Boolean007]
  Origin = -> Origin008
  Tip = -> Boolean007
COMPONENT P6 — recipe-attached ("door_fix1", modeled in this document).
Construction recipe (the document's own serialized feature program — sketch geometry with constraints, then the solid features built on it; lengths are millimeters unless a unit is written):

FEATURE [PartDesign::SubShapeBinder] Binder015
  BindCopyOnChange = 0
  BindMode = 0
  ClaimChildren = false
  Context = -> Body009 [Binder015.]
  Fuse = false
  MakeFace = true
  OffsetFill = false
  OffsetIntersection = false
  OffsetJoinType = 0
  OffsetOpenResult = false
  PartialLoad = false
  Relative = true
  Support = -> [Sketch046]
  _Version = 2
FEATURE [Sketcher::SketchObject] Sketch050
  AttachmentOffset = pos=(0,0,-13) rot=(0,0,1;0rad)
  ExternalGeometry = -> [Binder015]
  FullyConstrained = true
  MapMode = 5
  Placement = pos=(0,0,-13) rot=(0,0,1;0rad)
  sketch-geometry (4):
    g0: LineSegment StartX=-15 StartY=-1.8e-15 StartZ=0 EndX=15 EndY=3.091e-13 EndZ=0
    g1: ArcOfCircle CenterX=10 CenterY=23.1324 CenterZ=0 NormalX=0 NormalY=0 NormalZ=1 AngleXU=0 Radius=7 StartAngle=0.0322243 EndAngle=2.14272
    g2: ArcOfCircle CenterX=33.2738 CenterY=-13.0246 CenterZ=0 NormalX=0 NormalY=0 NormalZ=1 AngleXU=0 Radius=50 StartAngle=2.14272 EndAngle=2.87806
    g3: ArcOfCircle CenterX=-82.9517 CenterY=20.1361 CenterZ=0 NormalX=0 NormalY=0 NormalZ=1 AngleXU=0 Radius=100 StartAngle=6.08044 EndAngle=6.31541
  constraints (11):
    c: PointOnObject(g0,g-1)
    c: Symmetric(g0,g0,g-2)
    c: Coincident(g1,g-3)
    c: Coincident(g2,g0)
    c: Coincident(g3,g0)
    c: Tangent(g2,g1) = -1.5708
    c: Tangent(g3,g1) = -1.5708
    c: DistanceX(g0,g0) = 30
    c: Radius(g1) = 7
    c: Radius(g2) = 50
    c: Radius(g3) = 100
FEATURE [Sketcher::SketchObject] Sketch051
  AttachmentOffset = pos=(0,0,-7) rot=(0,0,1;0rad)
  ExternalGeometry = -> [Sketch050]
  FullyConstrained = true
  MapMode = 5
  Placement = pos=(0,0,-7) rot=(0,0,1;0rad)
  sketch-geometry (4):
    g0: ArcOfCircle CenterX=33.2738 CenterY=-13.0246 CenterZ=0 NormalX=0 NormalY=0 NormalZ=1 AngleXU=0 Radius=50 StartAngle=2.61743 EndAngle=2.87806
    g1: ArcOfCircle CenterX=-82.9517 CenterY=20.1361 CenterZ=0 NormalX=0 NormalY=0 NormalZ=1 AngleXU=0 Radius=100 StartAngle=6.08044 EndAngle=6.20173
    g2: LineSegment StartX=-10.0132 StartY=12 StartZ=0 EndX=16.7168 EndY=12 EndZ=0
    g3: LineSegment StartX=-15 StartY=-1.8e-15 StartZ=0 EndX=15 EndY=1.5419e-12 EndZ=0
  constraints (10):
    c: Coincident(g0,g-4)
    c: Coincident(g0,g-4)
    c: Coincident(g1,g-3)
    c: Coincident(g1,g-3)
    c: Coincident(g2,g0)
    c: Coincident(g2,g1)
    c: Horizontal(g2)
    c: DistanceY(g1) = 12
    c: Coincident(g3,g0)
    c: Coincident(g3,g1)
FEATURE [PartDesign::Pad] Pad013
  Direction = (0,0,1)
  Length = 6
  Length2 = 10
  Profile = -> Sketch050
  ReferenceAxis = -> Sketch050 [N_Axis]
  Suppressed = false
  Type = 0
  expr: Length = <<Sketch051>>.AttachmentOffset.Base.z - <<Sketch050>>.AttachmentOffset.Base.z
FEATURE [PartDesign::Pad] Pad014
  BaseFeature = -> Pad013
  Direction = (0,0,1)
  Length = 7
  Length2 = 10
  Profile = -> Sketch051
  ReferenceAxis = -> Sketch051 [N_Axis]
  Suppressed = false
  Type = 0
  expr: Length = -<<Sketch051>>.AttachmentOffset.Base.z
FEATURE [PartDesign::Plane] DatumPlane
  AttachmentOffset = pos=(0,0,7) rot=(0,0,1;0rad)
  Length = 60.4972
  MapMode = 5
  Placement = pos=(0,0,7) rot=(0,0,1;0rad)
  ResizeMode = 0
  Width = 65.5925
  expr: .AttachmentOffset.Base.z = <<Pad014>>.Length
FEATURE [PartDesign::Mirrored] Mirrored001
  BaseFeature = -> Pad014
  MirrorPlane = -> XY_Plane011
  Originals = -> [Pad014,Pad013]
  Suppressed = false
FEATURE [PartDesign::Pocket] Pocket005
  BaseFeature = -> Mirrored001
  Direction = (0,0,-1)
  Length = 5
  Length2 = 5
  Midplane = true
  Profile = -> Binder015
  Refine = true
  Suppressed = false
  Type = 1
FEATURE [PartDesign::CoordinateSystem] Local_CS022  label="door_rot_axis"
  AttacherType = Attacher::AttachEngine3D
  MapMode = 45
  Placement = pos=(10,23.1324,0) rot=(0,0,1;1.2e-05rad)
FEATURE [PartDesign::Boolean] Boolean009
  BaseFeature = -> Pocket005
  Group = -> [Compound017]
  Suppressed = false
  Type = 1
  UsePlacement = true
FEATURE [PartDesign::CoordinateSystem] Local_CS023  label="door_fix"
  AttacherType = Attacher::AttachEngine3D
  AttachmentOffset = pos=(0,0,0) rot=(0,1,0;3.14159rad)
  MapMode = 5
  Placement = pos=(0,0,0) rot=(0,0.707107,0.707107;3.14159rad)
FEATURE [PartDesign::Body] Body009  label="door_fix1"
  Group = -> [Sketch050,Binder015,Sketch051,Pad013,Pad014,DatumPlane,Mirrored001,Pocket005,Local_CS022,Boolean009,Local_CS023]
  Origin = -> Origin011
  Tip = -> Boolean009
COMPONENT P7 — recipe-attached ("door_fix2", modeled in this document).
Construction recipe (the document's own serialized feature program — sketch geometry with constraints, then the solid features built on it; lengths are millimeters unless a unit is written):

FEATURE [PartDesign::SubShapeBinder] Binder013
  BindCopyOnChange = 0
  BindMode = 0
  ClaimChildren = true
  Context = -> Body010 [Binder013.]
  Fuse = false
  MakeFace = true
  OffsetFill = false
  OffsetIntersection = false
  OffsetJoinType = 0
  OffsetOpenResult = false
  PartialLoad = false
  Relative = false
  Support = -> [Sketch048]
  _Version = 2
FEATURE [PartDesign::Pad] Pad012
  Direction = (0,0,1)
  Length = 13
  Length2 = 10
  Midplane = true
  Profile = -> Binder013
  Suppressed = false
  Type = 0
FEATURE [PartDesign::SubShapeBinder] Binder014
  BindCopyOnChange = 0
  BindMode = 0
  ClaimChildren = false
  Context = -> Body010 [Binder014.]
  Fuse = false
  MakeFace = true
  OffsetFill = false
  OffsetIntersection = false
  OffsetJoinType = 0
  OffsetOpenResult = false
  PartialLoad = false
  Relative = true
  Support = -> [Sketch049]
  _Version = 2
FEATURE [PartDesign::Pocket] Pocket004
  BaseFeature = -> Pad012
  Direction = (0,0,-1)
  Length = 5
  Length2 = 5
  Midplane = true
  Profile = -> Binder014
  Suppressed = false
  Type = 1
FEATURE [PartDesign::CoordinateSystem] Local_CS021  label="door_rot_axis2"
  AttacherType = Attacher::AttachEngine3D
  MapMode = 45
  Placement = pos=(8e-15,4.74044,0) rot=(0,0,1.16318;0rad)
FEATURE [PartDesign::Body] Body010  label="door_fix2"
  Group = -> [Binder013,Pad012,Binder014,Pocket004,Local_CS021]
  Origin = -> Origin012
  Tip = -> Pocket004
COMPONENT P8 — recipe-attached ("Body011", modeled in this document).
Construction recipe (the document's own serialized feature program — sketch geometry with constraints, then the solid features built on it; lengths are millimeters unless a unit is written):

FEATURE [Sketcher::SketchObject] Sketch052
  FullyConstrained = true
  MapMode = 5
  sketch-geometry (1):
    g0: Circle CenterX=0 CenterY=0 CenterZ=0 NormalX=0 NormalY=0 NormalZ=1 AngleXU=0 Radius=3.025
  constraints (2):
    c: Coincident(g0,g-1)
    c: Diameter(g0) = 6.05
FEATURE [Sketcher::SketchObject] Sketch053
  FullyConstrained = true
  MapMode = 5
  sketch-geometry (1):
    g0: Circle CenterX=0 CenterY=0 CenterZ=0 NormalX=0 NormalY=0 NormalZ=1 AngleXU=0 Radius=1.75
  constraints (2):
    c: Coincident(g0,g-1)
    c: Diameter(g0) = 3.5
FEATURE [PartDesign::Pad] Pad015
  Direction = (0,0,1)
  Length = 2.1
  Length2 = 10
  Profile = -> Sketch052
  ReferenceAxis = -> Sketch052 [N_Axis]
  Suppressed = false
  Type = 0
FEATURE [PartDesign::Pad] Pad016
  BaseFeature = -> Pad015
  Direction = (0,0,1)
  Length = 50
  Length2 = 10
  Profile = -> Sketch053
  ReferenceAxis = -> Sketch053 [N_Axis]
  Suppressed = false
  Type = 0
FEATURE [PartDesign::Body] Body011
  Group = -> [Sketch052,Sketch053,Pad015,Pad016]
  Origin = -> Origin013
  Tip = -> Pad016
COMPONENT P9 — recipe-attached ("lamp_fix", modeled in this document).
Construction recipe (the document's own serialized feature program — sketch geometry with constraints, then the solid features built on it; lengths are millimeters unless a unit is written):

FEATURE [PartDesign::SubShapeBinder] Binder016
  BindCopyOnChange = 0
  BindMode = 0
  ClaimChildren = true
  Context = -> Body012 [Binder016.]
  Fuse = false
  MakeFace = true
  OffsetFill = false
  OffsetIntersection = false
  OffsetJoinType = 0
  OffsetOpenResult = false
  PartialLoad = false
  Relative = false
  Support = -> [Sketch064]
  _Version = 2
FEATURE [PartDesign::FeaturePython] BaseBend004  label="lamp_fix_BaseBend"  # WARN: FeaturePython — macro-defined, semantics opaque (R4)
  BendSide = 0
  BendSketch = -> Binder016
  MidPlane = false
  Reverse = false
  Suppressed = false
  length = 900
  radius = 2
  thickness = 0.7
FEATURE [Sketcher::SketchObject] Sketch065  label="lamp_fix_cut_sketch"
  AttachmentOffset = pos=(0,166.7,0) rot=(0,1,0;1.5708rad)
  FullyConstrained = true
  MapMode = 7
  Placement = pos=(318.563,150.075,166.7) rot=(0.313146,0.671543,0.671543;2.53465rad)
  expr: .AttachmentOffset.Base.y = 60 mm + .Constraints.length / 2
  sketch-geometry (8):
    g0: LineSegment StartX=-0.5 StartY=-106.7 StartZ=0 EndX=2.2 EndY=-106.7 EndZ=0
    g1: LineSegment StartX=4.2 StartY=-104.7 StartZ=0 EndX=4.2 EndY=104.7 EndZ=0
    g2: LineSegment StartX=2.2 StartY=106.7 StartZ=0 EndX=-0.5 EndY=106.7 EndZ=0
    g3: LineSegment StartX=-0.5 StartY=106.7 StartZ=0 EndX=-0.5 EndY=-106.7 EndZ=0
    g4: ArcOfCircle CenterX=2.2 CenterY=104.7 CenterZ=0 NormalX=0 NormalY=0 NormalZ=1 AngleXU=0 Radius=2 StartAngle=-2.7e-15 EndAngle=1.5708
    g5: GeomPoint X=4.2 Y=106.7 Z=0
    g6: ArcOfCircle CenterX=2.2 CenterY=-104.7 CenterZ=0 NormalX=0 NormalY=0 NormalZ=1 AngleXU=0 Radius=2 StartAngle=4.71239 EndAngle=6.28319
    g7: GeomPoint X=4.2 Y=-106.7 Z=0
  constraints (19):
    c: Coincident(g2,g3)
    c: Horizontal(g0)
    c: Horizontal(g2)
    c: Vertical(g1)
    c: PointOnObject(g5,g1)
    c: PointOnObject(g5,g2)
    c: Tangent(g1,g4) = -1.5708
    c: Tangent(g2,g4) = -1.5708
    c: Tangent(g0,g6) = -1.5708
    c: Tangent(g1,g6) = -1.5708
    c: Equal(g6,g4)
    c: Radius(g6) = 2  'r'
    c: Coincident(g0,g3)
    c: DistanceX(g0) = -0.5
    c: PointOnObject(g7,g1)
    c: PointOnObject(g7,g0)
    c: Symmetric(g0,g2,g-1)
    c: DistanceY(g3,g3) = 213.4  'length'
    c: DistanceX(g0,g0) = 2.7
FEATURE [Sketcher::SketchObject] Sketch066  label="lamp_fix_cut_sketch2"
  AttachmentOffset = pos=(0,166.7,0) rot=(0,1,0;1.5708rad)
  FullyConstrained = true
  MapMode = 7
  Placement = pos=(299.412,134.005,166.7) rot=(0.889126,0.323616,0.323616;1.68804rad)
  expr: .AttachmentOffset.Base.y = <<lamp_fix_cut_sketch>>.AttachmentOffset.Base.y
  expr: Constraints[6] = <<lamp_fix_cut_sketch>>.Constraints.length
  expr: Constraints[7] = <<lamp_fix_cut_sketch>>.Constraints.r
  sketch-geometry (4):
    g0: ArcOfCircle CenterX=2 CenterY=108.7 CenterZ=0 NormalX=0 NormalY=0 NormalZ=1 AngleXU=0 Radius=2 StartAngle=3.14159 EndAngle=4.71239
    g1: ArcOfCircle CenterX=2 CenterY=-108.7 CenterZ=0 NormalX=0 NormalY=0 NormalZ=1 AngleXU=0 Radius=2 StartAngle=1.5708 EndAngle=3.14159
    g2: LineSegment StartX=0 StartY=-108.7 StartZ=0 EndX=0 EndY=108.7 EndZ=0
    g3: LineSegment StartX=2 StartY=106.7 StartZ=0 EndX=2 EndY=-106.7 EndZ=0
  constraints (10):
    c: Coincident(g0,g3)
    c: Perpendicular(g3,g1) = 4.71239
    c: Perpendicular(g0,g3)
    c: Tangent(g1,g2) = 1.5708
    c: Vertical(g2)
    c: Symmetric(g1,g0,g-1)
    c: DistanceY(g3,g3) = 213.4
    c: Radius(g1) = 2
    c: PointOnObject(g-1,g2)
    c: Tangent(g0,g2) = 1.5708
FEATURE [Sketcher::SketchObject] Sketch067
  AttachmentOffset = pos=(0,0,0) rot=(0,1,0;1.5708rad)
  FullyConstrained = true
  MapMode = 7
  Placement = pos=(299.412,134.005,0) rot=(0.889126,0.323616,0.323616;1.68804rad)
  sketch-geometry (3):
    g0: ArcOfCircle CenterX=3 CenterY=3 CenterZ=0 NormalX=0 NormalY=0 NormalZ=1 AngleXU=0 Radius=3 StartAngle=3.14159 EndAngle=4.71239
    g1: LineSegment StartX=0 StartY=3 StartZ=0 EndX=0 EndY=0 EndZ=0
    g2: LineSegment StartX=0 StartY=0 StartZ=0 EndX=3 EndY=0 EndZ=0
  constraints (7):
    c: Coincident(g1,g2)
    c: Tangent(g0,g1) = -1.5708
    c: Tangent(g2,g0) = -1.5708
    c: Coincident(g1,g-1)
    c: Vertical(g1)
    c: Horizontal(g2)
    c: Radius(g0) = 3
FEATURE [Sketcher::SketchObject] Sketch068
  AttachmentOffset = pos=(0,0,0) rot=(0,1,0;1.5708rad)
  FullyConstrained = true
  MapMode = 7
  Placement = pos=(263.568,197.924,0) rot=(-0.186157,0.694747,0.694747;3.50969rad)
  sketch-geometry (3):
    g0: LineSegment StartX=0 StartY=3 StartZ=0 EndX=0 EndY=0 EndZ=0
    g1: LineSegment StartX=0 StartY=0 StartZ=0 EndX=-3 EndY=0 EndZ=0
    g2: ArcOfCircle CenterX=-3 CenterY=3 CenterZ=0 NormalX=0 NormalY=0 NormalZ=1 AngleXU=0 Radius=3 StartAngle=4.71239 EndAngle=6.28319
  constraints (7):
    c: PointOnObject(g0,g-2)
    c: Coincident(g0,g-1)
    c: Coincident(g0,g1)
    c: Horizontal(g1)
    c: Tangent(g2,g0) = 1.5708
    c: Tangent(g2,g1) = 1.5708
    c: Radius(g2) = 3
FEATURE [PartDesign::Plane] DatumPlane002
  AttachmentOffset = pos=(0,0,450) rot=(0,0,1;0rad)
  Length = 399.987
  MapMode = 5
  Placement = pos=(0,0,450) rot=(0,0,1;0rad)
  ResizeMode = 0
  Width = 284.925
  expr: .AttachmentOffset.Base.z = <<lamp_fix_BaseBend>>.length / 2
FEATURE [PartDesign::Pocket] Pocket018
  BaseFeature = -> BaseBend004
  Direction = (-0.642788,0.766044,0)
  Length = 5
  Length2 = 5
  Profile = -> Sketch067
  ReferenceAxis = -> Sketch067 [N_Axis]
  Reversed = true
  Suppressed = false
  Type = 1
FEATURE [PartDesign::Pocket] Pocket019
  BaseFeature = -> Pocket018
  Direction = (0.5,-0.866025,0)
  Length = 5
  Length2 = 5
  Profile = -> Sketch068
  ReferenceAxis = -> Sketch068 [N_Axis]
  Reversed = true
  Suppressed = false
  Type = 0
FEATURE [PartDesign::Mirrored] Mirrored006
  BaseFeature = -> Pocket019
  MirrorPlane = -> DatumPlane002
  Originals = -> [Pocket018,Pocket019]
  Suppressed = false
FEATURE [PartDesign::CoordinateSystem] Local_CS026  label="lamp_fix_base_LCS"
  AttacherType = Attacher::AttachEngine3D
  MapMode = 5
FEATURE [PartDesign::CoordinateSystem] Local_CS028  label="lamp_fix_lamp_LCS"
  AttacherType = Attacher::AttachEngine3D
  MapMode = 2
  Placement = pos=(280.639,195.271,450) rot=(0.834817,-0.389282,-0.389282;1.75037rad)
FEATURE [PartDesign::Boolean] Boolean010
  BaseFeature = -> Mirrored006
  Group = -> [Compound018]
  Suppressed = false
  Type = 1
  UsePlacement = true
FEATURE [PartDesign::Body] Body012  label="lamp_fix"
  Group = -> [Binder016,BaseBend004,Sketch065,Sketch067,Sketch068,DatumPlane002,Pocket018,Pocket019,Mirrored006,Local_CS026,Sketch066,Boolean010,Local_CS028]
  Origin = -> Origin014
  Tip = -> Boolean010
COMPONENT P10 — recipe-attached ("lamp_fix_mirror", modeled in this document).
Construction recipe (the document's own serialized feature program — sketch geometry with constraints, then the solid features built on it; lengths are millimeters unless a unit is written):

FEATURE [PartDesign::SubShapeBinder] Binder017
  BindCopyOnChange = 0
  BindMode = 0
  ClaimChildren = true
  Context = -> Body013 [Binder017.]
  Fuse = false
  MakeFace = true
  OffsetFill = false
  OffsetIntersection = false
  OffsetJoinType = 0
  OffsetOpenResult = false
  PartialLoad = false
  Relative = true
  Support = -> [Part__Mirroring014]
  _Version = 2
FEATURE [PartDesign::FeaturePython] BaseBend005  # WARN: FeaturePython — macro-defined, semantics opaque (R4)
  BendSide = 1
  BendSketch = -> Binder017
  MidPlane = false
  Reverse = false
  Suppressed = false
  length = 900
  radius = 2
  thickness = 0.7
  expr: length = <<lamp_fix_BaseBend>>.length
  expr: radius = <<lamp_fix_BaseBend>>.radius
  expr: thickness = <<lamp_fix_BaseBend>>.thickness
FEATURE [PartDesign::Plane] DatumPlane003
  AttachmentOffset = pos=(0,0,450) rot=(0,0,1;0rad)
  Length = 399.511
  MapMode = 5
  Placement = pos=(0,0,450) rot=(0,0,1;0rad)
  ResizeMode = 0
  Width = 284.889
  expr: .AttachmentOffset.Base.z = <<BaseBend005>>.length / 2
FEATURE [Sketcher::SketchObject] Sketch069
  AttachmentOffset = pos=(0,0,0) rot=(0,1,0;1.5708rad)
  FullyConstrained = true
  MapMode = 7
  Placement = pos=(-299.412,134.005,0) rot=(0.249244,0.684791,0.684791;2.65306rad)
  sketch-geometry (3):
    g0: ArcOfCircle CenterX=3 CenterY=3 CenterZ=0 NormalX=0 NormalY=0 NormalZ=1 AngleXU=0 Radius=3 StartAngle=3.14159 EndAngle=4.71239
    g1: LineSegment StartX=2.6446e-12 StartY=3 StartZ=0 EndX=0 EndY=0 EndZ=0
    g2: LineSegment StartX=0 StartY=0 StartZ=0 EndX=3 EndY=2.6446e-12 EndZ=0
  constraints (7):
    c: Coincident(g1,g2)
    c: Tangent(g2,g0) = -1.5708
    c: Tangent(g0,g1) = -1.5708
    c: Coincident(g1,g-1)
    c: PointOnObject(g0,g-1)
    c: PointOnObject(g0,g-2)
    c: Radius(g0) = 3
FEATURE [Sketcher::SketchObject] Sketch070
  AttachmentOffset = pos=(0,0,0) rot=(0,1,0;1.5708rad)
  FullyConstrained = true
  MapMode = 7
  Placement = pos=(-263.568,197.924,0) rot=(0.935113,-0.250563,-0.250563;1.63783rad)
  sketch-geometry (3):
    g0: LineSegment StartX=-3 StartY=2.571e-13 StartZ=0 EndX=0 EndY=0 EndZ=0
    g1: LineSegment StartX=0 StartY=0 StartZ=0 EndX=0 EndY=3 EndZ=0
    g2: ArcOfCircle CenterX=-3 CenterY=3 CenterZ=0 NormalX=0 NormalY=0 NormalZ=1 AngleXU=0 Radius=3 StartAngle=4.71239 EndAngle=6.28319
  constraints (7):
    c: Coincident(g0,g-1)
    c: Coincident(g0,g1)
    c: Tangent(g2,g0) = -1.5708
    c: Tangent(g2,g1) = -1.5708
    c: Radius(g2) = 3
    c: PointOnObject(g1,g-2)
    c: PointOnObject(g0,g-1)
FEATURE [PartDesign::CoordinateSystem] Local_CS027
  AttacherType = Attacher::AttachEngine3D
  MapMode = 5
FEATURE [PartDesign::Pocket] Pocket027
  BaseFeature = -> BaseBend005
  Direction = (-0.642788,-0.766044,-2e-16)
  Length = 5
  Length2 = 5
  Midplane = true
  Profile = -> Sketch069
  ReferenceAxis = -> Sketch069 [N_Axis]
  Suppressed = false
  Type = 0
FEATURE [PartDesign::Pocket] Pocket021
  BaseFeature = -> Pocket027
  Direction = (0.5,0.866025,0)
  Length = 5
  Length2 = 5
  Midplane = true
  Profile = -> Sketch070
  ReferenceAxis = -> Sketch070 [N_Axis]
  Suppressed = false
  Type = 0
FEATURE [PartDesign::Mirrored] Mirrored007
  BaseFeature = -> Pocket021
  MirrorPlane = -> DatumPlane003
  Originals = -> [Pocket027,Pocket021]
  Suppressed = false
FEATURE [PartDesign::Boolean] Boolean011
  BaseFeature = -> Mirrored007
  Group = -> [Compound019]
  Suppressed = false
  Type = 1
  UsePlacement = true
FEATURE [PartDesign::Body] Body013  label="lamp_fix_mirror"
  Group = -> [Binder017,BaseBend005,DatumPlane003,Sketch069,Sketch070,Pocket027,Pocket021,Mirrored007,Boolean011,Local_CS027]
  Origin = -> Origin015
  Tip = -> Pocket027
COMPONENT P11 — recipe-attached ("Body016", modeled in this document).
Construction recipe (the document's own serialized feature program — sketch geometry with constraints, then the solid features built on it; lengths are millimeters unless a unit is written):

FEATURE [Sketcher::SketchObject] Sketch079
  FullyConstrained = true
  MapMode = 5
  sketch-geometry (5):
    g0: LineSegment StartX=-1.6 StartY=-50 StartZ=0 EndX=1.6 EndY=-50 EndZ=0
    g1: LineSegment StartX=1.6 StartY=-50 StartZ=0 EndX=1.6 EndY=50 EndZ=0
    g2: LineSegment StartX=1.6 StartY=50 StartZ=0 EndX=-1.6 EndY=50 EndZ=0
    g3: LineSegment StartX=-1.6 StartY=50 StartZ=0 EndX=-1.6 EndY=-50 EndZ=0
    g4: GeomPoint X=0 Y=0 Z=0
  constraints (12):
    c: Coincident(g0,g1)
    c: Coincident(g1,g2)
    c: Coincident(g2,g3)
    c: Coincident(g3,g0)
    c: Horizontal(g0)
    c: Horizontal(g2)
    c: Vertical(g1)
    c: Vertical(g3)
    c: Symmetric(g2,g0,g4)
    c: Coincident(g4,g-1)
    c: DistanceX(g0,g0) = 3.2
    c: DistanceY(g1,g1) = 100
FEATURE [PartDesign::Pad] Pad018
  Direction = (0,0,1)
  Length = 2.4
  Length2 = 10
  Profile = -> Sketch079
  ReferenceAxis = -> Sketch079 [N_Axis]
  Suppressed = false
  Type = 0
FEATURE [PartDesign::Boolean] Boolean015
  BaseFeature = -> Pad018
  Group = -> [Fusion002]
  Refine = true
  Suppressed = false
  Type = 0
  UsePlacement = true
FEATURE [PartDesign::Body] Body016
  Group = -> [Sketch079,Pad018,Boolean015]
  Origin = -> Origin018
  Tip = -> Boolean015
COMPONENT P12 — recipe-attached ("drain_holder", modeled in this document).
Construction recipe (the document's own serialized feature program — sketch geometry with constraints, then the solid features built on it; lengths are millimeters unless a unit is written):

FEATURE [PartDesign::SubShapeBinder] Binder021
  BindCopyOnChange = 0
  BindMode = 0
  ClaimChildren = true
  Context = -> Body017 [Binder021.]
  Fuse = false
  MakeFace = true
  OffsetFill = false
  OffsetIntersection = false
  OffsetJoinType = 0
  OffsetOpenResult = false
  PartialLoad = false
  Placement = pos=(0,0,-10) rot=(0,0,1;0rad)
  Relative = false
  Support = -> [Connect007]
  _Version = 2
FEATURE [PartDesign::FeaturePython] BaseBend006  label="drain_holder_BaseBend"  # WARN: FeaturePython — macro-defined, semantics opaque (R4)
  BendSide = 0
  BendSketch = -> Binder021
  MidPlane = false
  Reverse = false
  Suppressed = false
  length = 110
  radius = 0.1
  thickness = 0.3
FEATURE [PartDesign::CoordinateSystem] Local_CS033  label="drain_holder_LCS"
  AttacherType = Attacher::AttachEngine3D
  MapMode = 5
FEATURE [Sketcher::SketchObject] Sketch097
  AttachmentOffset = pos=(0,0,0) rot=(0,1,0;1.5708rad)
  FullyConstrained = true
  MapMode = 7
  Placement = pos=(86.1933,81.5915,-10) rot=(0.889126,-0.323616,-0.323616;1.68804rad)
  sketch-geometry (3):
    g0: ArcOfCircle CenterX=-5 CenterY=5 CenterZ=0 NormalX=0 NormalY=0 NormalZ=1 AngleXU=0 Radius=5 StartAngle=4.71239 EndAngle=6.28319
    g1: LineSegment StartX=-5 StartY=6.505e-12 StartZ=0 EndX=0 EndY=0 EndZ=0
    g2: LineSegment StartX=0 StartY=0 StartZ=0 EndX=-6.505e-12 EndY=5 EndZ=0
  constraints (7):
    c: PointOnObject(g0,g-1)
    c: PointOnObject(g0,g-2)
    c: Coincident(g1,g2)
    c: Tangent(g2,g0) = -1.5708
    c: Tangent(g0,g1) = -1.5708
    c: Coincident(g1,g-1)
    c: Radius(g0) = 5
FEATURE [PartDesign::Plane] DatumPlane006
  AttachmentOffset = pos=(0,0,45) rot=(0,0,1;0rad)
  Length = 202.327
  MapMode = 5
  Placement = pos=(0,0,45) rot=(0,0,1;0rad)
  ResizeMode = 0
  Width = 159.94
  expr: .AttachmentOffset.Base.z = <<drain_holder_BaseBend>>.length / 2 + <<Binder021>>.Placement.Base.z
FEATURE [PartDesign::Pocket] Pocket029
  BaseFeature = -> BaseBend006
  Direction = (0.642788,0.766044,0)
  Length = 5
  Length2 = 5
  Midplane = true
  Profile = -> Sketch097
  ReferenceAxis = -> Sketch097 [N_Axis]
  Suppressed = false
  Type = 0
FEATURE [PartDesign::Mirrored] Mirrored010
  MirrorPlane = -> DatumPlane006
  Suppressed = false
FEATURE [PartDesign::Mirrored] Mirrored011
  MirrorPlane = -> YZ_Plane019
  Suppressed = false
FEATURE [PartDesign::MultiTransform] MultiTransform005
  BaseFeature = -> Pocket029
  Originals = -> [Pocket029]
  Refine = true
  Suppressed = false
  Transformations = -> [Mirrored010,Mirrored011]
FEATURE [PartDesign::Boolean] Boolean016
  BaseFeature = -> MultiTransform005
  Group = -> [Compound022]
  Suppressed = false
  Type = 1
  UsePlacement = true
FEATURE [PartDesign::Body] Body017  label="drain_holder"
  Group = -> [Binder021,BaseBend006,DatumPlane006,Pocket029,MultiTransform005,Mirrored010,Mirrored011,Boolean016,Local_CS033,Sketch097]
  Origin = -> Origin019
  Tip = -> Boolean016
COMPONENT P13 — recipe-attached ("cap_outer", modeled in this document).
Construction recipe (the document's own serialized feature program — sketch geometry with constraints, then the solid features built on it; lengths are millimeters unless a unit is written):

FEATURE [PartDesign::SubShapeBinder] Binder022
  BindCopyOnChange = 0
  BindMode = 0
  ClaimChildren = true
  Context = -> Body018 [Binder022.]
  Fuse = false
  MakeFace = true
  OffsetFill = false
  OffsetIntersection = false
  OffsetJoinType = 0
  OffsetOpenResult = false
  PartialLoad = false
  Relative = false
  Support = -> [Sketch081]
  _Version = 2
FEATURE [PartDesign::FeaturePython] BaseBend007  label="cap_outer_BaseBend"  # WARN: FeaturePython — macro-defined, semantics opaque (R4)
  BendSide = 1
  BendSketch = -> Binder022
  MidPlane = false
  Reverse = false
  Suppressed = false
  length = 50
  radius = 0.1
  thickness = 0.3
FEATURE [PartDesign::FeaturePython] Bend005  # WARN: FeaturePython — macro-defined, semantics opaque (R4)
  AutoMiter = false
  BaseFeature = -> BaseBend007
  BendType = 1
  LengthList = [155]
  LengthSpec = 1
  ReliefFactor = 0.7
  Suppressed = false
  UseReliefFactor = false
  angle = 90
  baseObject = -> BaseBend007 [Edge43,Edge29,Edge14]
  bendAList = [90]
  extend1 = 0
  extend2 = 0
  gap1 = 0
  gap2 = 0
  invert = true
  kfactor = 0.5
  length = 155
  maxExtendDist = 5
  minGap = 0.2
  minReliefGap = 1
  miterangle1 = 0
  miterangle2 = 0
  offset = 0
  radius = 0.1
  reliefType = 0
  reliefd = 1
  reliefw = 0.8
  sketchflip = false
  sketchinvert = false
  unfold = false
  expr: length = <<cap_outer_base_Sketch>>.Constraints.depth
  expr: radius = BaseBend007.radius
FEATURE [PartDesign::SubShapeBinder] Binder023
  BindCopyOnChange = 0
  BindMode = 0
  ClaimChildren = true
  Context = -> Body018 [Binder023.]
  Fuse = true
  MakeFace = true
  OffsetFill = false
  OffsetIntersection = false
  OffsetJoinType = 0
  OffsetOpenResult = false
  PartialLoad = false
  Placement = pos=(0,0,50) rot=(0,0,1;0rad)
  Relative = false
  Support = -> [Part__Mirroring019,Offset2D]
  _Version = 2
  expr: .Placement.Base.z = <<cap_outer_BaseBend>>.length
FEATURE [PartDesign::Pocket] Pocket025
  BaseFeature = -> Bend005
  Direction = (0,0,1)
  Length = 0.8
  Length2 = 5
  Midplane = true
  Profile = -> Binder023
  Refine = true
  Suppressed = false
  Type = 0
FEATURE [PartDesign::SubShapeBinder] Binder024
  BindCopyOnChange = 0
  BindMode = 0
  ClaimChildren = true
  Context = -> Body018 [Binder024.]
  Fuse = false
  MakeFace = true
  OffsetFill = false
  OffsetIntersection = false
  OffsetJoinType = 0
  OffsetOpenResult = false
  PartialLoad = false
  Placement = pos=(0,0,50) rot=(0,0,1;0rad)
  Relative = true
  Support = -> [CapCornerCut]
  _Version = 2
  expr: Placement = <<Binder023>>.Placement
FEATURE [PartDesign::Pocket] Pocket026
  BaseFeature = -> Pocket025
  Direction = (0,0,1)
  Length = 0.8
  Length2 = 5
  Midplane = true
  Profile = -> Binder024
  Suppressed = false
  Type = 0
  expr: Length = <<Pocket025>>.Length
FEATURE [PartDesign::CoordinateSystem] Local_CS030  label="cap_outer_LCS"
  AttacherType = Attacher::AttachEngine3D
  MapMode = 5
FEATURE [PartDesign::Boolean] Boolean017
  BaseFeature = -> Pocket026
  Group = -> [Compound023]
  Suppressed = false
  Type = 1
  UsePlacement = true
FEATURE [PartDesign::Body] Body018  label="cap_outer"
  Group = -> [Binder022,BaseBend007,Bend005,Binder023,Pocket025,Binder024,Pocket026,Boolean017,Local_CS030]
  Origin = -> Origin020
  Tip = -> Boolean017
COMPONENT P14 — recipe-attached ("cap_inner", modeled in this document).
Construction recipe (the document's own serialized feature program — sketch geometry with constraints, then the solid features built on it; lengths are millimeters unless a unit is written):

FEATURE [PartDesign::SubShapeBinder] Binder025
  BindCopyOnChange = 0
  BindMode = 0
  ClaimChildren = true
  Context = -> Body019 [Binder025.]
  Fuse = false
  MakeFace = true
  OffsetFill = false
  OffsetIntersection = false
  OffsetJoinType = 0
  OffsetOpenResult = false
  PartialLoad = false
  Relative = false
  Support = -> [Sketch084]
  _Version = 2
FEATURE [PartDesign::FeaturePython] BaseBend008  label="cap_inner_BaseBend"  # WARN: FeaturePython — macro-defined, semantics opaque (R4)
  BendSide = 0
  BendSketch = -> Binder025
  MidPlane = false
  Placement = pos=(0,0,46.7) rot=(0,0,1;0rad)
  Reverse = false
  Suppressed = false
  length = 100
  radius = 0.1
  thickness = 0.3
  expr: .Placement.Base.z = <<cap_outer_BaseBend>>.length - 3.3 mm
FEATURE [PartDesign::FeaturePython] Bend006  # WARN: FeaturePython — macro-defined, semantics opaque (R4)
  AutoMiter = true
  BaseFeature = -> BaseBend008
  BendType = 1
  LengthList = [47]
  LengthSpec = 1
  ReliefFactor = 0.7
  Suppressed = false
  UseReliefFactor = false
  angle = 90
  baseObject = -> BaseBend008 [Edge13]
  bendAList = [90]
  extend1 = 0
  extend2 = 0
  gap1 = 0
  gap2 = 0
  invert = true
  kfactor = 0.5
  length = 47
  maxExtendDist = 5
  minGap = 0.2
  minReliefGap = 1
  miterangle1 = 0
  miterangle2 = 0
  offset = 0
  radius = 0.1
  reliefType = 0
  reliefd = 1
  reliefw = 0.8
  sketchflip = false
  sketchinvert = false
  unfold = false
  expr: length = <<cap_outer_BaseBend>>.length - 3 mm
  expr: radius = BaseBend008.radius
FEATURE [PartDesign::SubShapeBinder] Binder026
  BindCopyOnChange = 0
  BindMode = 0
  ClaimChildren = false
  Context = -> Body019 [Binder026.]
  Fuse = false
  MakeFace = true
  OffsetFill = false
  OffsetIntersection = false
  OffsetJoinType = 0
  OffsetOpenResult = false
  PartialLoad = false
  Relative = true
  Support = -> [Sketch027[Edge3]]
  _Version = 2
FEATURE [Sketcher::SketchObject] Sketch085
  AttachmentOffset = pos=(0,0,636.126) rot=(0,0,1;0rad)
  ExternalGeometry = -> [Binder026]
  FullyConstrained = true
  MapMode = 5
  Placement = pos=(636.126,0,0) rot=(0.57735,0.57735,0.57735;2.0944rad)
  expr: .AttachmentOffset.Base.z = <<cap_inner_sketch>>.Constraints.side
  sketch-geometry (8):
    g0: LineSegment StartX=72.8253 StartY=0 StartZ=0 EndX=72.8253 EndY=-2 EndZ=0
    g1: LineSegment StartX=72.8253 StartY=-2 StartZ=0 EndX=70.3253 EndY=-4.5 EndZ=0
    g2: LineSegment StartX=70.3253 StartY=-4.5 StartZ=0 EndX=61.3253 EndY=-4.5 EndZ=0
    g3: LineSegment StartX=61.3253 StartY=-4.5 StartZ=0 EndX=58.8253 EndY=-2 EndZ=0
    g4: LineSegment StartX=58.8253 StartY=-2 StartZ=0 EndX=58.8253 EndY=0 EndZ=0
    g5: LineSegment StartX=72.8253 StartY=0 StartZ=0 EndX=58.8253 EndY=0 EndZ=0
    g6: LineSegment StartX=75.8253 StartY=0 StartZ=0 EndX=72.8253 EndY=0 EndZ=0
    g7: LineSegment StartX=58.8253 StartY=0 StartZ=0 EndX=55.8253 EndY=0 EndZ=0
  constraints (22):
    c: Vertical(g0)
    c: Coincident(g0,g1)
    c: Coincident(g1,g2)
    c: Horizontal(g2)
    c: Coincident(g2,g3)
    c: Coincident(g3,g4)
    c: Vertical(g4)
    c: Equal(g4,g0)
    c: Equal(g1,g3)
    c: DistanceY(g2,g4) = 4.5
    c: DistanceY(g4,g4) = 2
    c: Coincident(g0,g5)
    c: Coincident(g5,g4)
    c: PointOnObject(g4,g-3)
    c: PointOnObject(g0,g-3)
    c: Coincident(g6,g-3)
    c: Coincident(g6,g0)
    c: Coincident(g7,g4)
    c: Coincident(g7,g-3)
    c: Equal(g7,g6)
    c: DistanceX(g7,g4) = 3
    c: Angle(g3) = 2.35619
FEATURE [PartDesign::CoordinateSystem] Local_CS031  label="cap_inner_LCS"
  AttacherType = Attacher::AttachEngine3D
  MapMode = 5
FEATURE [PartDesign::FeaturePython] Bend011  # WARN: FeaturePython — macro-defined, semantics opaque (R4)
  AutoMiter = true
  BaseFeature = -> Bend006
  BendType = 0
  LengthList = [40]
  LengthSpec = 0
  ReliefFactor = 0.7
  Suppressed = false
  UseReliefFactor = false
  angle = 90
  baseObject = -> Bend006 [Edge12]
  bendAList = [90]
  extend1 = 0
  extend2 = 0
  gap1 = 20
  gap2 = 3
  invert = true
  kfactor = 0.5
  length = 40
  maxExtendDist = 5
  minGap = 0.2
  minReliefGap = 1
  miterangle1 = 0
  miterangle2 = 0
  offset = 0
  radius = 0.1
  reliefType = 0
  reliefd = 1
  reliefw = 0.8
  sketchflip = false
  sketchinvert = false
  unfold = false
  expr: radius = <<cap_outer_BaseBend>>.radius
FEATURE [PartDesign::FeaturePython] Bend012  # WARN: FeaturePython — macro-defined, semantics opaque (R4)
  AutoMiter = true
  BaseFeature = -> Bend011
  BendType = 0
  LengthList = [20]
  LengthSpec = 0
  ReliefFactor = 0.7
  Suppressed = false
  UseReliefFactor = false
  angle = 90
  baseObject = -> Bend011 [Edge12]
  bendAList = [90]
  extend1 = 0
  extend2 = 0
  gap1 = 0
  gap2 = 3.2
  invert = true
  kfactor = 0.5
  length = 20
  maxExtendDist = 5
  minGap = 0.2
  minReliefGap = 1
  miterangle1 = 0
  miterangle2 = 0
  offset = 0
  radius = 0.1
  reliefType = 0
  reliefd = 1
  reliefw = 0.8
  sketchflip = false
  sketchinvert = false
  unfold = false
  expr: radius = <<cap_outer_BaseBend>>.radius
FEATURE [PartDesign::Boolean] Boolean018
  BaseFeature = -> Bend012
  Group = -> [Compound024]
  Suppressed = false
  Type = 1
  UsePlacement = true
FEATURE [PartDesign::Pad] Pad019
  BaseFeature = -> Boolean018
  Direction = (1,0,0)
  Length = 0.3
  Length2 = 10
  Profile = -> Sketch085
  ReferenceAxis = -> Sketch085 [N_Axis]
  Refine = true
  Reversed = true
  Suppressed = false
  Type = 0
FEATURE [PartDesign::Body] Body019  label="cap_inner"
  Group = -> [Binder025,BaseBend008,Bend006,Bend011,Bend012,Boolean018,Sketch085,Binder026,Pad019,Local_CS031]
  Origin = -> Origin021
  Tip = -> Pad019
COMPONENT P15 — recipe-attached ("top_triangle", modeled in this document).
Construction recipe (the document's own serialized feature program — sketch geometry with constraints, then the solid features built on it; lengths are millimeters unless a unit is written):

FEATURE [PartDesign::SubShapeBinder] Binder027
  BindCopyOnChange = 0
  BindMode = 0
  ClaimChildren = true
  Context = -> Body020 [Binder027.]
  Fuse = false
  MakeFace = true
  OffsetFill = false
  OffsetIntersection = false
  OffsetJoinType = 0
  OffsetOpenResult = false
  PartialLoad = false
  Relative = true
  Support = -> [Sketch088]
  _Version = 2
FEATURE [PartDesign::Pad] Pad020
  Direction = (0,0,1)
  Length = 0.3
  Length2 = 10
  Profile = -> Binder027
  Suppressed = false
  Type = 0
FEATURE [PartDesign::Boolean] Boolean020
  BaseFeature = -> Pad020
  Group = -> [Compound027]
  Suppressed = false
  Type = 1
  UsePlacement = true
FEATURE [PartDesign::Body] Body020  label="top_triangle"
  Group = -> [Binder027,Pad020,Boolean020]
  Origin = -> Origin022
  Tip = -> Boolean020
COMPONENT P16 — recipe-attached ("electric_shield", modeled in this document).
Construction recipe (the document's own serialized feature program — sketch geometry with constraints, then the solid features built on it; lengths are millimeters unless a unit is written):

FEATURE [PartDesign::SubShapeBinder] Binder028
  BindCopyOnChange = 0
  BindMode = 0
  ClaimChildren = true
  Context = -> Body021 [Binder028.]
  Fuse = false
  MakeFace = true
  OffsetFill = false
  OffsetIntersection = false
  OffsetJoinType = 0
  OffsetOpenResult = false
  PartialLoad = false
  Relative = false
  Support = -> [Sketch089]
  _Version = 2
FEATURE [PartDesign::FeaturePython] BaseBend009  # WARN: FeaturePython — macro-defined, semantics opaque (R4)
  BendSide = 0
  BendSketch = -> Binder028
  MidPlane = false
  Reverse = false
  Suppressed = false
  length = 100
  radius = 0.1
  thickness = 0.3
FEATURE [PartDesign::FeaturePython] Bend007  # WARN: FeaturePython — macro-defined, semantics opaque (R4)
  AutoMiter = false
  BaseFeature = -> BaseBend009
  BendType = 1
  LengthList = [30]
  LengthSpec = 1
  ReliefFactor = 0.7
  Suppressed = false
  UseReliefFactor = false
  angle = 90
  baseObject = -> BaseBend009 [Edge6,Edge9,Edge3,Edge11]
  bendAList = [90]
  extend1 = 0
  extend2 = 0
  gap1 = 0
  gap2 = 0
  invert = false
  kfactor = 0.5
  length = 30
  maxExtendDist = 5
  minGap = 0.2
  minReliefGap = 1
  miterangle1 = 0
  miterangle2 = 0
  offset = 0
  radius = 0.1
  reliefType = 0
  reliefd = 1
  reliefw = 0.8
  sketchflip = false
  sketchinvert = false
  unfold = false
  expr: radius = BaseBend009.radius
FEATURE [PartDesign::CoordinateSystem] Local_CS035  label="electric_shield_LCS"
  AttacherType = Attacher::AttachEngine3D
  AttachmentOffset = pos=(0,0,33) rot=(0,0,1;0rad)
  AttachmentSupport = -> [XY_Plane023]
  MapMode = 5
  Placement = pos=(0,0,33) rot=(0,0,1;0rad)
  expr: .AttachmentOffset.Base.z = <<Bend007>>.length + 3 mm
FEATURE [PartDesign::Boolean] Boolean021
  BaseFeature = -> Bend007
  Group = -> [Compound029]
  Suppressed = false
  Type = 1
  UsePlacement = true
FEATURE [PartDesign::Body] Body021  label="electric_shield"
  Group = -> [Binder028,BaseBend009,Bend007,Local_CS035,Boolean021]
  Origin = -> Origin023
  Tip = -> Boolean021
COMPONENT P17 — recipe-attached ("Body022", modeled in this document).
Construction recipe (the document's own serialized feature program — sketch geometry with constraints, then the solid features built on it; lengths are millimeters unless a unit is written):

FEATURE [PartDesign::SubShapeBinder] Binder029
  BindCopyOnChange = 0
  BindMode = 0
  ClaimChildren = true
  Context = -> Body022 [Binder029.]
  Fuse = false
  MakeFace = true
  OffsetFill = false
  OffsetIntersection = false
  OffsetJoinType = 0
  OffsetOpenResult = false
  PartialLoad = false
  Relative = true
  Support = -> [Offset2D001]
  _Version = 2
FEATURE [PartDesign::FeaturePython] BaseBend010  # WARN: FeaturePython — macro-defined, semantics opaque (R4)
  BendSide = 0
  BendSketch = -> Binder029
  MidPlane = false
  Reverse = true
  Suppressed = false
  length = 100
  radius = 0.1
  thickness = 0.3
FEATURE [PartDesign::FeaturePython] Bend008  # WARN: FeaturePython — macro-defined, semantics opaque (R4)
  AutoMiter = false
  BaseFeature = -> BaseBend010
  BendType = 0
  LengthList = [30]
  LengthSpec = 0
  ReliefFactor = 0.7
  Suppressed = false
  UseReliefFactor = false
  angle = 90
  baseObject = -> BaseBend010 [Edge15,Edge18,Edge21,Edge23]
  bendAList = [90]
  extend1 = 0
  extend2 = 0
  gap1 = 3
  gap2 = 3
  invert = false
  kfactor = 0.5
  length = 30
  maxExtendDist = 5
  minGap = 0.2
  minReliefGap = 1
  miterangle1 = 45
  miterangle2 = 45
  offset = 0
  radius = 0.1
  reliefType = 0
  reliefd = 0.1
  reliefw = 0.8
  sketchflip = false
  sketchinvert = false
  unfold = false
  expr: radius = BaseBend010.radius
FEATURE [PartDesign::Boolean] Boolean019
  BaseFeature = -> Bend008
  Group = -> [Compound026]
  Suppressed = false
  Type = 1
  UsePlacement = true
FEATURE [PartDesign::Body] Body022
  Group = -> [Binder029,BaseBend010,Bend008,Boolean019]
  Origin = -> Origin024
  Tip = -> Boolean019
COMPONENT P18 — recipe-attached ("bottom_cut_Body", modeled in this document).
Construction recipe (the document's own serialized feature program — sketch geometry with constraints, then the solid features built on it; lengths are millimeters unless a unit is written):

FEATURE [PartDesign::SubShapeBinder] Binder030
  BindCopyOnChange = 0
  BindMode = 0
  ClaimChildren = true
  Context = -> Body023 [Binder030.]
  Fuse = false
  MakeFace = true
  OffsetFill = false
  OffsetIntersection = false
  OffsetJoinType = 0
  OffsetOpenResult = false
  PartialLoad = false
  Relative = false
  Support = -> [Sketch044]
  _Version = 2
FEATURE [PartDesign::Pad] Pad021
  Direction = (0,0,1)
  Length = 100
  Length2 = 10
  Profile = -> Binder030
  Suppressed = false
  Type = 0
FEATURE [PartDesign::SubShapeBinder] Binder031
  BindCopyOnChange = 0
  BindMode = 0
  ClaimChildren = true
  Context = -> Body023 [Binder031.]
  Fuse = false
  MakeFace = true
  OffsetFill = false
  OffsetIntersection = false
  OffsetJoinType = 0
  OffsetOpenResult = false
  PartialLoad = false
  Placement = pos=(0,0,100) rot=(0,0,1;0rad)
  Relative = false
  Support = -> [Sketch093]
  _Version = 2
  expr: .Placement.Base.z = <<Pad021>>.Length
FEATURE [PartDesign::Pocket] Pocket028
  BaseFeature = -> Pad021
  Direction = (0,0,-1)
  Length = 30
  Length2 = 5
  Profile = -> Binder031
  Suppressed = false
  Type = 0
FEATURE [PartDesign::Fillet] Fillet
  Base = -> Pocket028 [Edge14]
  BaseFeature = -> Pocket028
  Radius = 5
  SupportTransform = false
  Suppressed = false
  UseAllEdges = false
FEATURE [PartDesign::Body] Body023  label="bottom_cut_Body"
  Group = -> [Binder030,Pad021,Binder031,Pocket028,Fillet]
  Origin = -> Origin025
  Placement = pos=(319.563,0,0) rot=(0,0,1;0rad)
  Tip = -> Fillet
  expr: .Placement.Base.x = <<mid_Sketch>>.Constraints.middle
COMPONENT P19 — recipe-attached ("drain_holder_back", modeled in this document).
Construction recipe (the document's own serialized feature program — sketch geometry with constraints, then the solid features built on it; lengths are millimeters unless a unit is written):

FEATURE [PartDesign::SubShapeBinder] Binder033
  BindCopyOnChange = 0
  BindMode = 0
  ClaimChildren = true
  Context = -> Body025 [Binder033.]
  Fuse = false
  MakeFace = true
  OffsetFill = false
  OffsetIntersection = false
  OffsetJoinType = 0
  OffsetOpenResult = false
  PartialLoad = false
  Placement = pos=(0,101.6,0) rot=(1,0,0;1.5708rad)
  Relative = false
  Support = -> [Sketch098]
  _Version = 2
  expr: .Placement.Base.y = <<drain_holder_base_sketch>>.Constraints.offset - 3.4 mm
FEATURE [PartDesign::FeaturePython] BaseBend012  # WARN: FeaturePython — macro-defined, semantics opaque (R4)
  BendSide = 0
  BendSketch = -> Binder033
  MidPlane = false
  Reverse = false
  Suppressed = false
  length = 80
  radius = 0.1
  thickness = 0.3
FEATURE [PartDesign::FeaturePython] Bend013  # WARN: FeaturePython — macro-defined, semantics opaque (R4)
  AutoMiter = true
  BaseFeature = -> BaseBend012
  BendType = 0
  LengthList = [20]
  LengthSpec = 0
  ReliefFactor = 0.7
  Suppressed = false
  UseReliefFactor = false
  angle = 90
  baseObject = -> BaseBend012 [Edge32,Edge3]
  bendAList = [90]
  extend1 = 0
  extend2 = 0
  gap1 = 4
  gap2 = 4
  invert = false
  kfactor = 0.5
  length = 20
  maxExtendDist = 5
  minGap = 0.2
  minReliefGap = 1
  miterangle1 = 0
  miterangle2 = 0
  offset = 0
  radius = 0.1
  reliefType = 0
  reliefd = 1
  reliefw = 0.8
  sketchflip = false
  sketchinvert = false
  unfold = false
  expr: radius = BaseBend012.radius
FEATURE [Sketcher::SketchObject] Sketch099
  ExternalGeometry = -> [Binder033]
  FullyConstrained = true
  MapMode = 5
  Placement = pos=(0,0,0) rot=(0.57735,0.57735,0.57735;2.0944rad)
  expr: Constraints[8] = <<BaseBend012>>.length
  sketch-geometry (3):
    g0: LineSegment StartX=21.6 StartY=57 StartZ=0 EndX=98.6 EndY=15 EndZ=0
    g1: LineSegment StartX=98.6 StartY=15 StartZ=0 EndX=21.6 EndY=15 EndZ=0
    g2: LineSegment StartX=21.6 StartY=15 StartZ=0 EndX=21.6 EndY=57 EndZ=0
  constraints (9):
    c: Coincident(g0,g1)
    c: Horizontal(g1)
    c: Coincident(g1,g2)
    c: Coincident(g2,g0)
    c: Vertical(g2)
    c: Horizontal(g0,g-3)
    c: DistanceX(g0,g-3) = 3
    c: DistanceY(g0,g-3) = 3
    c: DistanceX(g1,g-3) = 80
FEATURE [PartDesign::Pocket] Pocket030
  BaseFeature = -> Bend013
  Direction = (-1,0,0)
  Length = 5
  Length2 = 5
  Midplane = true
  Profile = -> Sketch099
  ReferenceAxis = -> Sketch099 [N_Axis]
  Suppressed = false
  Type = 1
FEATURE [PartDesign::CoordinateSystem] Local_CS036
  AttacherType = Attacher::AttachEngine3D
  MapMode = 5
FEATURE [PartDesign::Boolean] Boolean022
  BaseFeature = -> Pocket030
  Group = -> [Compound030]
  Suppressed = false
  Type = 1
  UsePlacement = true
FEATURE [PartDesign::Body] Body025  label="drain_holder_back"
  Group = -> [Binder033,BaseBend012,Bend013,Sketch099,Pocket030,Local_CS036,Boolean022]
  Origin = -> Origin027
  Tip = -> Pocket030
COMPONENT P20 — recipe-attached ("basin_shield_wall", modeled in this document).
Construction recipe (the document's own serialized feature program — sketch geometry with constraints, then the solid features built on it; lengths are millimeters unless a unit is written):

FEATURE [PartDesign::SubShapeBinder] Binder034
  BindCopyOnChange = 0
  BindMode = 0
  ClaimChildren = true
  Context = -> Body026 [Binder034.]
  Fuse = false
  MakeFace = true
  OffsetFill = false
  OffsetIntersection = false
  OffsetJoinType = 0
  OffsetOpenResult = false
  PartialLoad = false
  Relative = true
  Support = -> [Connect009]
  _Version = 2
FEATURE [PartDesign::FeaturePython] BaseBend013  # WARN: FeaturePython — macro-defined, semantics opaque (R4)
  BendSide = 0
  BendSketch = -> Binder034
  MidPlane = false
  Reverse = false
  Suppressed = false
  length = 245
  radius = 0.1
  thickness = 0.3
FEATURE [PartDesign::FeaturePython] Extend002  # WARN: FeaturePython — macro-defined, semantics opaque (R4)
  BaseFeature = -> BaseBend013
  Offset = 0.02
  Refine = true
  Suppressed = false
  UseSubtraction = false
  baseObject = -> BaseBend013 [Face1]
  gap1 = 0
  gap2 = 0
  length = 0
FEATURE [PartDesign::FeaturePython] Bend014  # WARN: FeaturePython — macro-defined, semantics opaque (R4)
  AutoMiter = true
  BaseFeature = -> Extend002
  BendType = 0
  LengthList = [20]
  LengthSpec = 1
  ReliefFactor = 0.7
  Suppressed = false
  UseReliefFactor = false
  angle = 90
  baseObject = -> Extend002 [Edge73,Edge58,Edge76,Edge29,Edge14]
  bendAList = [90]
  extend1 = 0
  extend2 = 0
  gap1 = 0
  gap2 = 0
  invert = false
  kfactor = 0.5
  length = 20
  maxExtendDist = 5
  minGap = 0.2
  minReliefGap = 1
  miterangle1 = 0
  miterangle2 = 0
  offset = 0
  radius = 0.1
  reliefType = 0
  reliefd = 1
  reliefw = 0.8
  sketchflip = false
  sketchinvert = false
  unfold = false
  expr: radius = BaseBend013.radius
FEATURE [Sketcher::SketchObject] Sketch108
  FullyConstrained = true
  MapMode = 5
  Placement = pos=(0,0,0) rot=(0.57735,0.57735,0.57735;2.0944rad)
  sketch-geometry (11):
    g0: LineSegment StartX=0 StartY=0 StartZ=0 EndX=40 EndY=0 EndZ=0
    g1: LineSegment StartX=40 StartY=0 StartZ=0 EndX=40 EndY=70 EndZ=0
    g2: LineSegment StartX=40 StartY=70 StartZ=0 EndX=0 EndY=70 EndZ=0
    g3: LineSegment StartX=0 StartY=70 StartZ=0 EndX=0 EndY=0 EndZ=0
    g4: LineSegment StartX=50 StartY=0 StartZ=0 EndX=0 EndY=0 EndZ=0
    g5: LineSegment StartX=0 StartY=0 StartZ=0 EndX=0 EndY=80 EndZ=0
    g6: ArcOfCircle CenterX=10 CenterY=80 CenterZ=0 NormalX=0 NormalY=0 NormalZ=1 AngleXU=0 Radius=10 StartAngle=3.14159 EndAngle=4.71239
    g7: ArcOfCircle CenterX=50 CenterY=10 CenterZ=0 NormalX=0 NormalY=0 NormalZ=1 AngleXU=0 Radius=10 StartAngle=3.14159 EndAngle=4.71239
    g8: ArcOfCircle CenterX=-314.75 CenterY=10 CenterZ=0 NormalX=0 NormalY=0 NormalZ=1 AngleXU=0 Radius=354.75 StartAngle=2e-16 EndAngle=0.142615
    g9: ArcOfCircle CenterX=26.5 CenterY=59 CenterZ=0 NormalX=0 NormalY=0 NormalZ=1 AngleXU=0 Radius=10 StartAngle=0.142615 EndAngle=1.44973
    g10: ArcOfCircle CenterX=10 CenterY=-76.625 CenterZ=0 NormalX=0 NormalY=0 NormalZ=1 AngleXU=0 Radius=146.625 StartAngle=1.44973 EndAngle=1.5708
  constraints (28):
    c: Coincident(g0,g1)
    c: Coincident(g1,g2)
    c: Coincident(g2,g3)
    c: Coincident(g3,g0)
    c: Horizontal(g0)
    c: Horizontal(g2)
    c: Vertical(g1)
    c: Vertical(g3)
    c: Distance(g1,g3) = 40
    c: Distance(g0,g2) = 70
    c: Coincident(g0,g-1)
    c: PointOnObject(g4,g-1)
    c: Coincident(g4,g0)
    c: Coincident(g4,g5)
    c: PointOnObject(g5,g-2)
    c: Tangent(g6,g5) = 1.5708
    c: Tangent(g7,g4) = 1.5708
    c: Tangent(g8,g7) = 1.5708
    c: Tangent(g10,g6) = 1.5708
    c: Tangent(g10,g9) = -1.5708
    c: Tangent(g9,g8) = -1.5708
    c: Equal(g6,g7)
    c: Radius(g6) = 10
    c: Tangent(g7,g1) = 1.5708
    c: Tangent(g6,g2) = 1.5708
    c: Equal(g9,g6)
    c: DistanceX(g9) = 26.5
    c: DistanceY(g9) = 59
FEATURE [PartDesign::Pocket] Pocket031
  BaseFeature = -> Bend014
  Direction = (-1,0,0)
  Length = 5
  Length2 = 5
  Midplane = true
  Profile = -> Sketch108
  ReferenceAxis = -> Sketch108 [N_Axis]
  Suppressed = false
  Type = 1
FEATURE [PartDesign::Boolean] Boolean024
  BaseFeature = -> Pocket031
  Group = -> [Compound032]
  Suppressed = false
  Type = 1
  UsePlacement = true
FEATURE [PartDesign::Body] Body026  label="basin_shield_wall"
  Group = -> [Binder034,BaseBend013,Extend002,Bend014,Sketch108,Pocket031,Boolean024]
  Origin = -> Origin028
  Tip = -> Boolean024
COMPONENT P21 — recipe-attached ("basin_shield_top", modeled in this document).
Construction recipe (the document's own serialized feature program — sketch geometry with constraints, then the solid features built on it; lengths are millimeters unless a unit is written):

FEATURE [PartDesign::SubShapeBinder] Binder035
  BindCopyOnChange = 0
  BindMode = 0
  ClaimChildren = true
  Context = -> Body027 [Binder035.]
  Fuse = false
  MakeFace = true
  OffsetFill = false
  OffsetIntersection = false
  OffsetJoinType = 0
  OffsetOpenResult = false
  PartialLoad = false
  Relative = true
  Support = -> [Connect010]
  _Version = 2
FEATURE [PartDesign::FeaturePython] BaseBend014  # WARN: FeaturePython — macro-defined, semantics opaque (R4)
  BendSide = 0
  BendSketch = -> Binder035
  MidPlane = false
  Reverse = false
  Suppressed = false
  length = 100
  radius = 0.1
  thickness = 0.3
FEATURE [PartDesign::Boolean] Boolean023
  BaseFeature = -> BaseBend014
  Group = -> [Compound031]
  Refine = true
  Suppressed = false
  Type = 1
  UsePlacement = true
FEATURE [PartDesign::FeaturePython] Bend015  # WARN: FeaturePython — macro-defined, semantics opaque (R4)
  AutoMiter = false
  BaseFeature = -> Boolean023
  BendType = 0
  LengthList = [25]
  LengthSpec = 0
  ReliefFactor = 0.7
  Suppressed = false
  UseReliefFactor = false
  angle = 90
  baseObject = -> Boolean023 [Edge15,Edge17,Edge19]
  bendAList = [90]
  extend1 = 0
  extend2 = 0
  gap1 = 2.5
  gap2 = 2.5
  invert = false
  kfactor = 0.5
  length = 25
  maxExtendDist = 5
  minGap = 0.2
  minReliefGap = 1
  miterangle1 = 30
  miterangle2 = 30
  offset = 0
  radius = 0.1
  reliefType = 0
  reliefd = 1
  reliefw = 0.8
  sketchflip = false
  sketchinvert = false
  unfold = false
  expr: radius = BaseBend014.radius
FEATURE [PartDesign::Boolean] Boolean027
  BaseFeature = -> Bend015
  Group = -> [Compound035]
  Suppressed = false
  Type = 1
  UsePlacement = true
FEATURE [PartDesign::Body] Body027  label="basin_shield_top"
  Group = -> [Binder035,BaseBend014,Boolean023,Bend015,Boolean027]
  Origin = -> Origin029
  Tip = -> Boolean027
COMPONENT P22 — recipe-attached ("basin_shield_corrugation", modeled in this document).
Construction recipe (the document's own serialized feature program — sketch geometry with constraints, then the solid features built on it; lengths are millimeters unless a unit is written):

FEATURE [PartDesign::SubShapeBinder] Binder038
  BindCopyOnChange = 0
  BindMode = 0
  ClaimChildren = true
  Context = -> Body030 [Binder038.]
  Fuse = false
  MakeFace = true
  OffsetFill = false
  OffsetIntersection = false
  OffsetJoinType = 0
  OffsetOpenResult = false
  PartialLoad = false
  Relative = true
  Support = -> [Connect012]
  _Version = 2
FEATURE [PartDesign::FeaturePython] BaseBend017  # WARN: FeaturePython — macro-defined, semantics opaque (R4)
  BendSide = 0
  BendSketch = -> Binder038
  MidPlane = false
  Reverse = false
  Suppressed = false
  length = 262
  radius = 0.1
  thickness = 0.3
FEATURE [PartDesign::FeaturePython] Extend003  # WARN: FeaturePython — macro-defined, semantics opaque (R4)
  BaseFeature = -> BaseBend017
  Offset = 0.02
  Refine = true
  Suppressed = false
  UseSubtraction = false
  baseObject = -> BaseBend017 [Face1]
  gap1 = 0
  gap2 = 0
  length = 0
FEATURE [PartDesign::Boolean] Boolean028
  BaseFeature = -> Extend003
  Group = -> [Compound036]
  Suppressed = false
  Type = 1
  UsePlacement = true
FEATURE [PartDesign::Body] Body030  label="basin_shield_corrugation"
  Group = -> [Binder038,BaseBend017,Extend003,Boolean028]
  Origin = -> Origin032
  Tip = -> Boolean028
COMPONENT P23 — recipe-attached ("Body", modeled in this document).
Construction recipe (the document's own serialized feature program — sketch geometry with constraints, then the solid features built on it; lengths are millimeters unless a unit is written):

FEATURE [PartDesign::SubShapeBinder] Binder039
  BindCopyOnChange = 0
  BindMode = 0
  ClaimChildren = false
  Context = -> Body031 [Binder039.]
  Fuse = false
  MakeFace = true
  OffsetFill = false
  OffsetIntersection = false
  OffsetJoinType = 0
  OffsetOpenResult = false
  PartialLoad = false
  Relative = true
  Support = -> [Connect013]
  _Version = 2
FEATURE [PartDesign::Pad] Pad022
  Direction = (0,0,1)
  Length = 1
  Length2 = 10
  Profile = -> Binder039
  Refine = true
  Suppressed = false
  Type = 0
FEATURE [PartDesign::Boolean] Boolean029
  BaseFeature = -> Pad022
  Group = -> [Compound037]
  Suppressed = false
  Type = 1
  UsePlacement = true
FEATURE [PartDesign::Body] Body031  label="Body"
  Group = -> [Binder039,Pad022,Boolean029]
  Origin = -> Origin033
  Tip = -> Boolean029
COMPONENT P24 — recipe-attached ("Body032", modeled in this document).
Construction recipe (the document's own serialized feature program — sketch geometry with constraints, then the solid features built on it; lengths are millimeters unless a unit is written):

FEATURE [PartDesign::SubShapeBinder] Binder041
  BindCopyOnChange = 0
  BindMode = 0
  ClaimChildren = true
  Context = -> Body032 [Binder041.]
  Fuse = false
  MakeFace = true
  OffsetFill = false
  OffsetIntersection = false
  OffsetJoinType = 0
  OffsetOpenResult = false
  PartialLoad = false
  Relative = false
  Support = -> [Sketch124]
  _Version = 2
FEATURE [PartDesign::FeaturePython] BaseBend022  # WARN: FeaturePython — macro-defined, semantics opaque (R4)
  BendSide = 0
  BendSketch = -> Binder041
  MidPlane = false
  Reverse = false
  Suppressed = false
  length = 900
  radius = 1
  thickness = 4
  expr: length = <<BaseBend023>>.length
FEATURE [PartDesign::Boolean] Boolean033
  BaseFeature = -> BaseBend022
  Group = -> [Compound042]
  Suppressed = false
  Type = 1
  UsePlacement = true
FEATURE [PartDesign::Body] Body032
  Group = -> [Binder041,BaseBend022,Boolean033]
  Origin = -> Origin034
  Tip = -> Boolean033
COMPONENT P25 — recipe-attached ("Body033", modeled in this document).
Construction recipe (the document's own serialized feature program — sketch geometry with constraints, then the solid features built on it; lengths are millimeters unless a unit is written):

FEATURE [PartDesign::SubShapeBinder] Binder042
  BindCopyOnChange = 0
  BindMode = 0
  ClaimChildren = true
  Context = -> Body033 [Binder042.]
  Fuse = false
  MakeFace = true
  OffsetFill = false
  OffsetIntersection = false
  OffsetJoinType = 0
  OffsetOpenResult = false
  PartialLoad = false
  Relative = false
  Support = -> [Sketch120]
  _Version = 2
FEATURE [PartDesign::FeaturePython] BaseBend023  # WARN: FeaturePython — macro-defined, semantics opaque (R4)
  BendSide = 0
  BendSketch = -> Binder042
  MidPlane = false
  Reverse = false
  Suppressed = false
  length = 900
  radius = 1
  thickness = 1
FEATURE [PartDesign::Boolean] Boolean032
  BaseFeature = -> BaseBend023
  Group = -> [Fusion008]
  Suppressed = false
  Type = 1
  UsePlacement = true
FEATURE [PartDesign::Body] Body033
  Group = -> [Binder042,BaseBend023,Boolean032]
  Origin = -> Origin035
  Tip = -> Boolean032
COMPONENT P26 — recipe-attached ("Body034", modeled in this document).
Construction recipe (the document's own serialized feature program — sketch geometry with constraints, then the solid features built on it; lengths are millimeters unless a unit is written):

FEATURE [PartDesign::SubShapeBinder] Binder043
  BindCopyOnChange = 0
  BindMode = 0
  ClaimChildren = true
  Context = -> Body034 [Binder043.]
  Fuse = false
  MakeFace = true
  OffsetFill = false
  OffsetIntersection = false
  OffsetJoinType = 0
  OffsetOpenResult = false
  PartialLoad = false
  Relative = false
  Support = -> [Connect014]
  _Version = 2
  expr: Support = Connect014._self
FEATURE [PartDesign::Pad] Pad023
  Direction = (-0.642788,0.766044,0)
  Length = 3
  Length2 = 10
  Midplane = true
  Profile = -> Binder043 [Face1]
  Suppressed = false
  Type = 0
FEATURE [PartDesign::SubShapeBinder] Binder044
  BindCopyOnChange = 0
  BindMode = 0
  ClaimChildren = true
  Context = -> Body034 [Binder044.]
  Fuse = false
  MakeFace = true
  OffsetFill = false
  OffsetIntersection = false
  OffsetJoinType = 0
  OffsetOpenResult = false
  PartialLoad = false
  Relative = false
  Support = -> [Connect015]
  _Version = 2
FEATURE [PartDesign::Pad] Pad024
  BaseFeature = -> Pad023
  Direction = (0.707107,0.707107,0)
  Length = 3
  Length2 = 10
  Midplane = true
  Profile = -> Binder044
  Refine = true
  Suppressed = false
  Type = 0
FEATURE [PartDesign::Body] Body034
  Group = -> [Binder043,Pad023,Binder044,Pad024]
  Origin = -> Origin036
  Tip = -> Pad024
